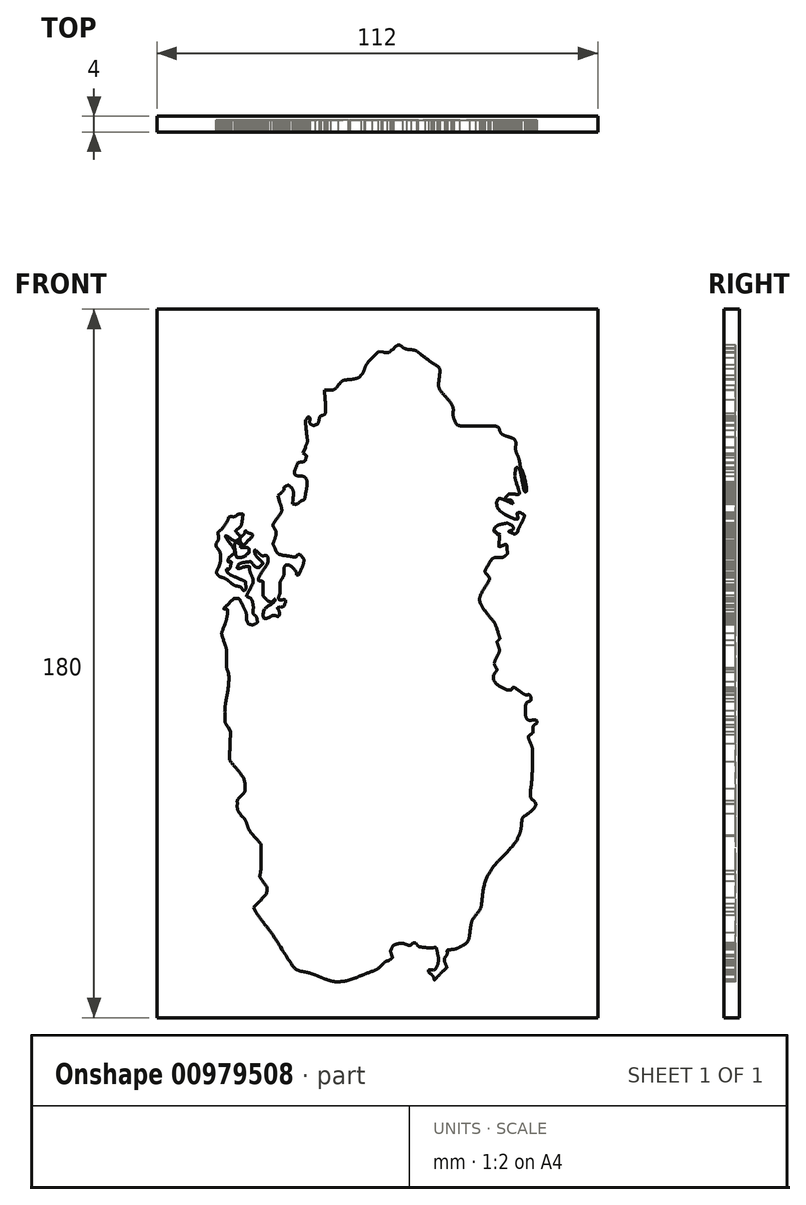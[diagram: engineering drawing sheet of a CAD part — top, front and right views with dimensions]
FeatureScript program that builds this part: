
annotation { "Feature Type Name" : "Feature", "Feature Type Description" : "" }
export const myFeature = defineFeature(function(context is Context, id is Id, definition is map)
    precondition{}
    {
        {
            var Q0;
            Q0=qCreatedBy(makeId("Front.planeOp"),FACE);
            var sketch = newSketch(context, id + "F0", { "sketchPlane" : qUnion([Q0])});
            skLineSegment(sketch, "E0.bottom", {"start": v(56, -90) * mm, "end": v(-56, -90) * mm});
            skLineSegment(sketch, "E0.top", {"start": v(56, 90) * mm, "end": v(-56, 90) * mm});
            skLineSegment(sketch, "E0.left", {"start": v(56, -90) * mm, "end": v(56, 90) * mm});
            skLineSegment(sketch, "E0.right", {"start": v(-56, -90) * mm, "end": v(-56, 90) * mm});
            skPoint(sketch, "E0.middle", {"position": v(0, 0) * mm});
            skLineSegment(sketch, "E1", {"start": v(-32.88, 19.2) * mm, "end": v(-32.1, 20.83) * mm});
            skLineSegment(sketch, "E2", {"start": v(-32.1, 20.83) * mm, "end": v(-32.57, 22.16) * mm});
            skLineSegment(sketch, "E3", {"start": v(-27.5, 16.63) * mm, "end": v(-26.83, 16.28) * mm});
            skLineSegment(sketch, "E4", {"start": v(-26.83, 16.28) * mm, "end": v(-26.97, 16.83) * mm});
            skLineSegment(sketch, "E5", {"start": v(-24.85, 15.67) * mm, "end": v(-25.4, 15.88) * mm});
            skLineSegment(sketch, "E6", {"start": v(-25.4, 15.88) * mm, "end": v(-25.34, 18.4) * mm});
            skLineSegment(sketch, "E7", {"start": v(-1.75, 78.04) * mm, "end": v(-0.2, 79.6) * mm});
            skLineSegment(sketch, "E8", {"start": v(-0.2, 79.6) * mm, "end": v(1.27, 79.6) * mm});
            skLineSegment(sketch, "E9", {"start": v(38.3, 44.26) * mm, "end": v(38.3, 43.17) * mm});
            skLineSegment(sketch, "E10", {"start": v(38.3, 43.17) * mm, "end": v(37.62, 43.24) * mm});
            skLineSegment(sketch, "E11", {"start": v(39.65, -31.25) * mm, "end": v(39.52, -33.83) * mm});
            skLineSegment(sketch, "E12", {"start": v(39.52, -33.83) * mm, "end": v(40.18, -34.42) * mm});
            skLineSegment(sketch, "E13", {"start": v(1.4, 79.08) * mm, "end": v(0.3, 79.22) * mm});
            skLineSegment(sketch, "E14", {"start": v(0.3, 79.22) * mm, "end": v(-1.23, 77.67) * mm});
            skLineSegment(sketch, "E15", {"start": v(-12.51, 69.45) * mm, "end": v(-13.4, 69.45) * mm});
            skLineSegment(sketch, "E16", {"start": v(-13.4, 69.45) * mm, "end": v(-13.27, 67.07) * mm});
            skLineSegment(sketch, "E17", {"start": v(-18.31, 54.9) * mm, "end": v(-18.88, 53.48) * mm});
            skLineSegment(sketch, "E18", {"start": v(-18.88, 53.48) * mm, "end": v(-18.43, 53.1) * mm});
            skLineSegment(sketch, "E19", {"start": v(-20.94, 40.45) * mm, "end": v(-21.55, 40.45) * mm});
            skLineSegment(sketch, "E20", {"start": v(-21.55, 40.45) * mm, "end": v(-21.44, 41.8) * mm});
            skLineSegment(sketch, "E21", {"start": v(-24.47, 43.3) * mm, "end": v(-25.23, 42.61) * mm});
            skLineSegment(sketch, "E22", {"start": v(-25.23, 42.61) * mm, "end": v(-24.8, 41.05) * mm});
            skLineSegment(sketch, "E23", {"start": v(-37.96, -16.18) * mm, "end": v(-37.29, -17.23) * mm});
            skLineSegment(sketch, "E24", {"start": v(-37.29, -17.23) * mm, "end": v(-37.41, -20.41) * mm});
            skLineSegment(sketch, "E25", {"start": v(-30.4, -60.92) * mm, "end": v(-31.42, -62.04) * mm});
            skLineSegment(sketch, "E26", {"start": v(-31.42, -62.04) * mm, "end": v(-30.9, -63.02) * mm});
            skLineSegment(sketch, "E27", {"start": v(-36.35, 33.14) * mm, "end": v(-36.7, 33.88) * mm});
            skLineSegment(sketch, "E28", {"start": v(-36.7, 33.88) * mm, "end": v(-35.92, 34.57) * mm});
            skLineSegment(sketch, "E29", {"start": v(-34.09, 31.43) * mm, "end": v(-34.09, 30.84) * mm});
            skLineSegment(sketch, "E30", {"start": v(-34.09, 30.84) * mm, "end": v(-33.35, 31.56) * mm});
            skFitSpline(sketch, "E31", {"points": [v(-13.45, -80.7) * mm, v(-14.26, -80.4) * mm, v(-15.79, -79.86) * mm, v(-16.84, -79.51) * mm]});
            skFitSpline(sketch, "E32", {"points": [v(-16.84, -79.51) * mm, v(-20.43, -78.33) * mm, v(-20.6, -78.25) * mm, v(-21.55, -77.26) * mm]});
            skFitSpline(sketch, "E33", {"points": [v(-21.55, -77.26) * mm, v(-22.07, -76.72) * mm, v(-23.66, -74.52) * mm, v(-25.09, -72.37) * mm]});
            skFitSpline(sketch, "E34", {"points": [v(-25.09, -72.37) * mm, v(-26.52, -70.21) * mm, v(-28.36, -67.6) * mm, v(-29.19, -66.55) * mm]});
            skFitSpline(sketch, "E35", {"points": [v(-29.19, -66.55) * mm, v(-30.6, -64.76) * mm, v(-31.97, -62.53) * mm, v(-31.97, -62.03) * mm]});
            skFitSpline(sketch, "E36", {"points": [v(-31.97, -62.03) * mm, v(-31.97, -61.91) * mm, v(-31.5, -61.27) * mm, v(-30.92, -60.6) * mm]});
            skFitSpline(sketch, "E37", {"points": [v(-30.92, -60.6) * mm, v(-29.85, -59.39) * mm, v(-29, -57.92) * mm, v(-29, -57.28) * mm]});
            skFitSpline(sketch, "E38", {"points": [v(-29, -57.28) * mm, v(-29, -57.08) * mm, v(-29.34, -56.3) * mm, v(-29.75, -55.53) * mm]});
            skFitSpline(sketch, "E39", {"points": [v(-29.75, -55.53) * mm, v(-30.57, -53.98) * mm, v(-30.63, -53.57) * mm, v(-30.2, -52.72) * mm]});
            skFitSpline(sketch, "E40", {"points": [v(-30.2, -52.72) * mm, v(-29.95, -52.26) * mm, v(-29.92, -51.55) * mm, v(-30.04, -49.29) * mm]});
            skFitSpline(sketch, "E41", {"points": [v(-30.04, -49.29) * mm, v(-30.2, -46.13) * mm, v(-30.12, -46.32) * mm, v(-32.34, -43.6) * mm]});
            skFitSpline(sketch, "E42", {"points": [v(-32.34, -43.6) * mm, v(-32.83, -43) * mm, v(-33.38, -42.01) * mm, v(-33.55, -41.42) * mm]});
            skFitSpline(sketch, "E43", {"points": [v(-33.55, -41.42) * mm, v(-33.73, -40.84) * mm, v(-34.2, -39.94) * mm, v(-34.62, -39.44) * mm]});
            skFitSpline(sketch, "E44", {"points": [v(-34.62, -39.44) * mm, v(-36.03, -37.71) * mm, v(-36.52, -35.97) * mm, v(-35.98, -34.56) * mm]});
            skFitSpline(sketch, "E45", {"points": [v(-35.98, -34.56) * mm, v(-35.86, -34.24) * mm, v(-35.38, -33.57) * mm, v(-34.92, -33.07) * mm]});
            skFitSpline(sketch, "E46", {"points": [v(-34.92, -33.07) * mm, v(-33.97, -32.03) * mm, v(-34, -32.17) * mm, v(-34.37, -30.78) * mm]});
            skFitSpline(sketch, "E47", {"points": [v(-34.37, -30.78) * mm, v(-34.75, -29.38) * mm, v(-35.2, -28.53) * mm, v(-36.46, -26.88) * mm]});
            skFitSpline(sketch, "E48", {"points": [v(-36.46, -26.88) * mm, v(-37.04, -26.13) * mm, v(-37.61, -25.27) * mm, v(-37.73, -24.97) * mm]});
            skFitSpline(sketch, "E49", {"points": [v(-37.73, -24.97) * mm, v(-37.97, -24.39) * mm, v(-38.06, -21.07) * mm, v(-37.9, -18.8) * mm]});
            skFitSpline(sketch, "E50", {"points": [v(-37.9, -18.8) * mm, v(-37.82, -17.55) * mm, v(-37.87, -17.35) * mm, v(-38.39, -16.67) * mm]});
            skFitSpline(sketch, "E51", {"points": [v(-38.39, -16.67) * mm, v(-39.51, -15.19) * mm, v(-39.6, -12.77) * mm, v(-38.72, -7.81) * mm]});
            skFitSpline(sketch, "E52", {"points": [v(-38.72, -7.81) * mm, v(-38.24, -5.14) * mm, v(-38.31, -2.1) * mm, v(-38.87, -1) * mm]});
            skFitSpline(sketch, "E53", {"points": [v(-38.87, -1) * mm, v(-39.1, -0.56) * mm, v(-39.11, -0.29) * mm, v(-38.94, 0.17) * mm]});
            skFitSpline(sketch, "E54", {"points": [v(-38.94, 0.17) * mm, v(-38.62, 1) * mm, v(-38.87, 3.38) * mm, v(-39.5, 5.38) * mm]});
            skFitSpline(sketch, "E55", {"points": [v(-39.5, 5.38) * mm, v(-39.78, 6.29) * mm, v(-40.01, 7.26) * mm, v(-40.01, 7.54) * mm]});
            skFitSpline(sketch, "E56", {"points": [v(-40.01, 7.54) * mm, v(-40.01, 7.83) * mm, v(-39.68, 9.05) * mm, v(-39.27, 10.27) * mm]});
            skFitSpline(sketch, "E57", {"points": [v(-39.27, 10.27) * mm, v(-38.41, 12.85) * mm, v(-38.39, 13.06) * mm, v(-38.96, 13.2) * mm]});
            skFitSpline(sketch, "E58", {"points": [v(-38.96, 13.2) * mm, v(-39.71, 13.4) * mm, v(-39.48, 14.32) * mm, v(-38.38, 15.5) * mm]});
            skFitSpline(sketch, "E59", {"points": [v(-38.38, 15.5) * mm, v(-36.83, 17.16) * mm, v(-35.68, 17.57) * mm, v(-34.74, 16.8) * mm]});
            skFitSpline(sketch, "E60", {"points": [v(-34.74, 16.8) * mm, v(-34.08, 16.26) * mm, v(-32.77, 13.22) * mm, v(-32.66, 11.98) * mm]});
            skFitSpline(sketch, "E61", {"points": [v(-32.66, 11.98) * mm, v(-32.55, 10.86) * mm, v(-32.37, 10.61) * mm, v(-31.6, 10.6) * mm]});
            skFitSpline(sketch, "E62", {"points": [v(-31.6, 10.6) * mm, v(-31, 10.6) * mm, v(-30.96, 11.24) * mm, v(-31.55, 11.77) * mm]});
            skFitSpline(sketch, "E63", {"points": [v(-31.55, 11.77) * mm, v(-31.84, 12.03) * mm, v(-31.97, 12.42) * mm, v(-31.97, 13) * mm]});
            skFitSpline(sketch, "E64", {"points": [v(-31.97, 13) * mm, v(-31.97, 14.32) * mm, v(-32.62, 16.12) * mm, v(-33.18, 16.38) * mm]});
            skFitSpline(sketch, "E65", {"points": [v(-33.18, 16.38) * mm, v(-33.86, 16.69) * mm, v(-33.8, 17.27) * mm, v(-32.88, 19.2) * mm]});
            skFitSpline(sketch, "E66", {"points": [v(-32.57, 22.16) * mm, v(-32.82, 22.9) * mm, v(-33.03, 23.65) * mm, v(-33.03, 23.83) * mm]});
            skFitSpline(sketch, "E67", {"points": [v(-33.03, 23.83) * mm, v(-33.03, 24.1) * mm, v(-33.14, 24.14) * mm, v(-33.5, 24.01) * mm]});
            skFitSpline(sketch, "E68", {"points": [v(-33.5, 24.01) * mm, v(-33.77, 23.92) * mm, v(-34.4, 23.84) * mm, v(-34.93, 23.84) * mm]});
            skFitSpline(sketch, "E69", {"points": [v(-34.93, 23.84) * mm, v(-35.84, 23.83) * mm, v(-35.89, 23.86) * mm, v(-35.95, 24.48) * mm]});
            skFitSpline(sketch, "E70", {"points": [v(-35.95, 24.48) * mm, v(-36.05, 25.55) * mm, v(-34.78, 26.27) * mm, v(-32.78, 26.27) * mm]});
            skFitSpline(sketch, "E71", {"points": [v(-32.78, 26.27) * mm, v(-31.93, 26.27) * mm, v(-31.64, 26.16) * mm, v(-31.1, 25.65) * mm]});
            skFitSpline(sketch, "E72", {"points": [v(-31.1, 25.65) * mm, v(-30.75, 25.3) * mm, v(-30.32, 25.08) * mm, v(-30.15, 25.14) * mm]});
            skFitSpline(sketch, "E73", {"points": [v(-30.15, 25.14) * mm, v(-29.7, 25.31) * mm, v(-29.77, 25.47) * mm, v(-30.7, 26.37) * mm]});
            skFitSpline(sketch, "E74", {"points": [v(-30.7, 26.37) * mm, v(-31.5, 27.15) * mm, v(-31.55, 27.27) * mm, v(-31.55, 28.43) * mm]});
            skFitSpline(sketch, "E75", {"points": [v(-31.55, 28.43) * mm, v(-31.55, 29.6) * mm, v(-31.52, 29.65) * mm, v(-31.02, 29.65) * mm]});
            skFitSpline(sketch, "E76", {"points": [v(-31.02, 29.65) * mm, v(-30.7, 29.65) * mm, v(-30.49, 29.53) * mm, v(-30.49, 29.36) * mm]});
            skFitSpline(sketch, "E77", {"points": [v(-30.49, 29.36) * mm, v(-30.49, 28.94) * mm, v(-28.82, 27.75) * mm, v(-28.24, 27.75) * mm]});
            skFitSpline(sketch, "E78", {"points": [v(-28.24, 27.75) * mm, v(-27.83, 27.75) * mm, v(-27.75, 27.6) * mm, v(-27.62, 26.6) * mm]});
            skFitSpline(sketch, "E79", {"points": [v(-27.62, 26.6) * mm, v(-27.46, 25.26) * mm, v(-27.66, 24.55) * mm, v(-28.57, 23.22) * mm]});
            skFitSpline(sketch, "E80", {"points": [v(-28.57, 23.22) * mm, v(-29.21, 22.29) * mm, v(-29.4, 21.61) * mm, v(-29.02, 21.61) * mm]});
            skFitSpline(sketch, "E81", {"points": [v(-29.02, 21.61) * mm, v(-28.66, 21.61) * mm, v(-28.35, 20.18) * mm, v(-28.49, 19.14) * mm]});
            skFitSpline(sketch, "E82", {"points": [v(-28.49, 19.14) * mm, v(-28.66, 17.84) * mm, v(-28.36, 17.07) * mm, v(-27.5, 16.63) * mm]});
            skFitSpline(sketch, "E83", {"points": [v(-26.97, 16.83) * mm, v(-27.1, 17.33) * mm, v(-27.05, 17.38) * mm, v(-26.5, 17.38) * mm]});
            skFitSpline(sketch, "E84", {"points": [v(-26.5, 17.38) * mm, v(-25.81, 17.38) * mm, v(-25.62, 17.08) * mm, v(-25.62, 16.04) * mm]});
            skFitSpline(sketch, "E85", {"points": [v(-25.62, 16.04) * mm, v(-25.62, 15.5) * mm, v(-25.82, 15.19) * mm, v(-26.56, 14.52) * mm]});
            skFitSpline(sketch, "E86", {"points": [v(-26.56, 14.52) * mm, v(-27.09, 14.05) * mm, v(-27.58, 13.4) * mm, v(-27.66, 13.06) * mm]});
            skFitSpline(sketch, "E87", {"points": [v(-27.66, 13.06) * mm, v(-27.79, 12.49) * mm, v(-27.76, 12.45) * mm, v(-27.3, 12.58) * mm]});
            skFitSpline(sketch, "E88", {"points": [v(-27.3, 12.58) * mm, v(-27.01, 12.65) * mm, v(-26.47, 12.72) * mm, v(-26.09, 12.72) * mm]});
            skFitSpline(sketch, "E89", {"points": [v(-26.09, 12.72) * mm, v(-25.47, 12.72) * mm, v(-25.42, 12.76) * mm, v(-25.61, 13.13) * mm]});
            skFitSpline(sketch, "E90", {"points": [v(-25.61, 13.13) * mm, v(-26.02, 13.88) * mm, v(-25.88, 14.6) * mm, v(-25.31, 14.75) * mm]});
            skFitSpline(sketch, "E91", {"points": [v(-25.31, 14.75) * mm, v(-25.03, 14.82) * mm, v(-24.68, 15.01) * mm, v(-24.55, 15.17) * mm]});
            skFitSpline(sketch, "E92", {"points": [v(-24.55, 15.17) * mm, v(-24.35, 15.4) * mm, v(-24.42, 15.5) * mm, v(-24.85, 15.67) * mm]});
            skFitSpline(sketch, "E93", {"points": [v(-25.34, 18.4) * mm, v(-25.28, 20.49) * mm, v(-25.2, 21.05) * mm, v(-24.84, 21.66) * mm]});
            skFitSpline(sketch, "E94", {"points": [v(-24.84, 21.66) * mm, v(-24.6, 22.07) * mm, v(-24.33, 22.91) * mm, v(-24.25, 23.54) * mm]});
            skFitSpline(sketch, "E95", {"points": [v(-24.25, 23.54) * mm, v(-24.05, 24.98) * mm, v(-23.67, 25.42) * mm, v(-22.64, 25.42) * mm]});
            skFitSpline(sketch, "E96", {"points": [v(-22.64, 25.42) * mm, v(-21.97, 25.42) * mm, v(-21.73, 25.28) * mm, v(-21.09, 24.54) * mm]});
            skFitSpline(sketch, "E97", {"points": [v(-21.09, 24.54) * mm, v(-20.67, 24.05) * mm, v(-20.32, 23.55) * mm, v(-20.32, 23.43) * mm]});
            skFitSpline(sketch, "E98", {"points": [v(-20.32, 23.43) * mm, v(-20.3, 22.93) * mm, v(-19.5, 25.15) * mm, v(-19.5, 25.74) * mm]});
            skFitSpline(sketch, "E99", {"points": [v(-19.5, 25.74) * mm, v(-19.48, 26.68) * mm, v(-19.75, 27) * mm, v(-20.27, 26.68) * mm]});
            skFitSpline(sketch, "E100", {"points": [v(-20.27, 26.68) * mm, v(-20.84, 26.32) * mm, v(-23.7, 26.75) * mm, v(-24.99, 27.38) * mm]});
            skFitSpline(sketch, "E101", {"points": [v(-24.99, 27.38) * mm, v(-26.7, 28.23) * mm, v(-27.27, 29.95) * mm, v(-26.55, 32.07) * mm]});
            skFitSpline(sketch, "E102", {"points": [v(-26.55, 32.07) * mm, v(-26.23, 33) * mm, v(-26.23, 33.13) * mm, v(-26.58, 33.9) * mm]});
            skFitSpline(sketch, "E103", {"points": [v(-26.58, 33.9) * mm, v(-27.04, 34.91) * mm, v(-26.9, 36) * mm, v(-26.2, 36.92) * mm]});
            skFitSpline(sketch, "E104", {"points": [v(-26.2, 36.92) * mm, v(-24.96, 38.54) * mm, v(-24.76, 39.42) * mm, v(-25.3, 40.73) * mm]});
            skFitSpline(sketch, "E105", {"points": [v(-25.3, 40.73) * mm, v(-25.48, 41.15) * mm, v(-25.62, 41.87) * mm, v(-25.62, 42.33) * mm]});
            skFitSpline(sketch, "E106", {"points": [v(-25.62, 42.33) * mm, v(-25.62, 43.02) * mm, v(-25.5, 43.25) * mm, v(-24.99, 43.62) * mm]});
            skFitSpline(sketch, "E107", {"points": [v(-24.99, 43.62) * mm, v(-24.64, 43.87) * mm, v(-24.35, 44.26) * mm, v(-24.35, 44.48) * mm]});
            skFitSpline(sketch, "E108", {"points": [v(-24.35, 44.48) * mm, v(-24.35, 45.6) * mm, v(-22.43, 46.16) * mm, v(-21.62, 45.29) * mm]});
            skFitSpline(sketch, "E109", {"points": [v(-21.62, 45.29) * mm, v(-21.1, 44.74) * mm, v(-20.66, 42.78) * mm, v(-20.82, 41.8) * mm]});
            skFitSpline(sketch, "E110", {"points": [v(-20.82, 41.8) * mm, v(-20.95, 40.98) * mm, v(-20.5, 40.8) * mm, v(-20.12, 41.5) * mm]});
            skFitSpline(sketch, "E111", {"points": [v(-20.12, 41.5) * mm, v(-20, 41.74) * mm, v(-19.7, 41.93) * mm, v(-19.48, 41.93) * mm]});
            skFitSpline(sketch, "E112", {"points": [v(-19.48, 41.93) * mm, v(-19.2, 41.93) * mm, v(-19.03, 42.12) * mm, v(-18.95, 42.51) * mm]});
            skFitSpline(sketch, "E113", {"points": [v(-18.95, 42.51) * mm, v(-18.9, 42.83) * mm, v(-18.75, 43.5) * mm, v(-18.63, 44) * mm]});
            skFitSpline(sketch, "E114", {"points": [v(-18.63, 44) * mm, v(-18.15, 46.1) * mm, v(-18.46, 46.83) * mm, v(-19.95, 47.1) * mm]});
            skFitSpline(sketch, "E115", {"points": [v(-19.95, 47.1) * mm, v(-21.37, 47.35) * mm, v(-21.68, 48.31) * mm, v(-21.02, 50.45) * mm]});
            skFitSpline(sketch, "E116", {"points": [v(-21.02, 50.45) * mm, v(-20.67, 51.58) * mm, v(-20.6, 51.66) * mm, v(-20, 51.67) * mm]});
            skFitSpline(sketch, "E117", {"points": [v(-20, 51.67) * mm, v(-19.64, 51.67) * mm, v(-19.17, 51.8) * mm, v(-18.94, 51.97) * mm]});
            skFitSpline(sketch, "E118", {"points": [v(-18.94, 51.97) * mm, v(-18.56, 52.25) * mm, v(-18.55, 52.28) * mm, v(-18.9, 52.67) * mm]});
            skFitSpline(sketch, "E119", {"points": [v(-18.9, 52.67) * mm, v(-19.36, 53.18) * mm, v(-19.37, 53.99) * mm, v(-18.93, 55) * mm]});
            skFitSpline(sketch, "E120", {"points": [v(-18.93, 55) * mm, v(-18.26, 56.57) * mm, v(-18.22, 56.96) * mm, v(-18.55, 58.71) * mm]});
            skFitSpline(sketch, "E121", {"points": [v(-18.55, 58.71) * mm, v(-19.05, 61.35) * mm, v(-18.66, 63.1) * mm, v(-17.57, 63.1) * mm]});
            skFitSpline(sketch, "E122", {"points": [v(-17.57, 63.1) * mm, v(-17.13, 63.1) * mm, v(-16.93, 62.86) * mm, v(-16.62, 61.94) * mm]});
            skFitSpline(sketch, "E123", {"points": [v(-16.62, 61.94) * mm, v(-16.19, 60.62) * mm, v(-15.25, 61.36) * mm, v(-15.25, 63.03) * mm]});
            skFitSpline(sketch, "E124", {"points": [v(-15.25, 63.03) * mm, v(-15.25, 63.72) * mm, v(-15.21, 63.77) * mm, v(-14.72, 63.65) * mm]});
            skFitSpline(sketch, "E125", {"points": [v(-14.72, 63.65) * mm, v(-13.88, 63.44) * mm, v(-13.7, 64.21) * mm, v(-13.86, 67.25) * mm]});
            skFitSpline(sketch, "E126", {"points": [v(-13.86, 67.25) * mm, v(-14.01, 70.15) * mm, v(-14.06, 70.07) * mm, v(-12.21, 70.08) * mm]});
            skFitSpline(sketch, "E127", {"points": [v(-12.21, 70.08) * mm, v(-11.52, 70.08) * mm, v(-11.25, 70.23) * mm, v(-10.4, 71.12) * mm]});
            skFitSpline(sketch, "E128", {"points": [v(-10.4, 71.12) * mm, v(-9.38, 72.18) * mm, v(-9.03, 72.34) * mm, v(-6.52, 72.84) * mm]});
            skFitSpline(sketch, "E129", {"points": [v(-6.52, 72.84) * mm, v(-4.93, 73.15) * mm, v(-4.21, 73.78) * mm, v(-3.7, 75.27) * mm]});
            skFitSpline(sketch, "E130", {"points": [v(-3.7, 75.27) * mm, v(-3.38, 76.2) * mm, v(-2.96, 76.8) * mm, v(-1.75, 78.04) * mm]});
            skFitSpline(sketch, "E131", {"points": [v(1.27, 79.6) * mm, v(2.66, 79.6) * mm, v(2.79, 79.65) * mm, v(3.57, 80.36) * mm]});
            skFitSpline(sketch, "E132", {"points": [v(3.57, 80.36) * mm, v(4.72, 81.4) * mm, v(5.62, 81.51) * mm, v(6.84, 80.8) * mm]});
            skFitSpline(sketch, "E133", {"points": [v(6.84, 80.8) * mm, v(7.4, 80.48) * mm, v(8.11, 80.24) * mm, v(8.56, 80.24) * mm]});
            skFitSpline(sketch, "E134", {"points": [v(8.56, 80.24) * mm, v(9.65, 80.24) * mm, v(10.66, 79.76) * mm, v(12.03, 78.58) * mm]});
            skFitSpline(sketch, "E135", {"points": [v(12.03, 78.58) * mm, v(12.68, 78.02) * mm, v(13.76, 77.21) * mm, v(14.43, 76.8) * mm]});
            skFitSpline(sketch, "E136", {"points": [v(14.43, 76.8) * mm, v(16.07, 75.75) * mm, v(16.3, 75.23) * mm, v(16.26, 72.68) * mm]});
            skFitSpline(sketch, "E137", {"points": [v(16.26, 72.68) * mm, v(16.21, 70.3) * mm, v(16.3, 70.06) * mm, v(17.99, 67.97) * mm]});
            skFitSpline(sketch, "E138", {"points": [v(17.99, 67.97) * mm, v(19.34, 66.28) * mm, v(19.58, 65.73) * mm, v(19.78, 63.84) * mm]});
            skFitSpline(sketch, "E139", {"points": [v(19.78, 63.84) * mm, v(19.97, 61.97) * mm, v(20.1, 61.75) * mm, v(21.2, 61.28) * mm]});
            skFitSpline(sketch, "E140", {"points": [v(21.2, 61.28) * mm, v(21.95, 60.97) * mm, v(22.77, 60.9) * mm, v(25.95, 60.87) * mm]});
            skFitSpline(sketch, "E141", {"points": [v(25.95, 60.87) * mm, v(29.47, 60.83) * mm, v(29.87, 60.8) * mm, v(30.78, 60.35) * mm]});
            skFitSpline(sketch, "E142", {"points": [v(30.78, 60.35) * mm, v(31.33, 60.09) * mm, v(31.82, 59.71) * mm, v(31.88, 59.53) * mm]});
            skFitSpline(sketch, "E143", {"points": [v(31.88, 59.53) * mm, v(32.1, 58.78) * mm, v(32.32, 58.58) * mm, v(33.34, 58.19) * mm]});
            skFitSpline(sketch, "E144", {"points": [v(33.34, 58.19) * mm, v(35, 57.54) * mm, v(35.47, 56.96) * mm, v(35.61, 55.41) * mm]});
            skFitSpline(sketch, "E145", {"points": [v(35.61, 55.41) * mm, v(35.68, 54.7) * mm, v(35.93, 53.67) * mm, v(36.17, 53.15) * mm]});
            skFitSpline(sketch, "E146", {"points": [v(36.17, 53.15) * mm, v(36.4, 52.63) * mm, v(36.6, 51.94) * mm, v(36.6, 51.62) * mm]});
            skFitSpline(sketch, "E147", {"points": [v(36.6, 51.62) * mm, v(36.6, 51.3) * mm, v(36.8, 50.55) * mm, v(37.02, 49.93) * mm]});
            skFitSpline(sketch, "E148", {"points": [v(37.02, 49.93) * mm, v(37.7, 48.08) * mm, v(38.3, 45.42) * mm, v(38.3, 44.26) * mm]});
            skFitSpline(sketch, "E149", {"points": [v(37.62, 43.24) * mm, v(36.87, 43.31) * mm, v(36.86, 43.33) * mm, v(36.05, 46.9) * mm]});
            skFitSpline(sketch, "E150", {"points": [v(36.05, 46.9) * mm, v(35.75, 48.23) * mm, v(35.65, 48.45) * mm, v(35.6, 47.92) * mm]});
            skFitSpline(sketch, "E151", {"points": [v(35.6, 47.92) * mm, v(35.56, 47.55) * mm, v(35.72, 46.61) * mm, v(35.96, 45.84) * mm]});
            skFitSpline(sketch, "E152", {"points": [v(35.96, 45.84) * mm, v(36.2, 45.06) * mm, v(36.4, 44.16) * mm, v(36.4, 43.83) * mm]});
            skFitSpline(sketch, "E153", {"points": [v(36.4, 43.83) * mm, v(36.4, 42.72) * mm, v(36.23, 42.57) * mm, v(35.04, 42.57) * mm]});
            skFitSpline(sketch, "E154", {"points": [v(35.04, 42.57) * mm, v(34.35, 42.57) * mm, v(33.78, 42.44) * mm, v(33.53, 42.23) * mm]});
            skFitSpline(sketch, "E155", {"points": [v(33.53, 42.23) * mm, v(33.14, 41.92) * mm, v(33.15, 41.9) * mm, v(33.78, 42.01) * mm]});
            skFitSpline(sketch, "E156", {"points": [v(33.78, 42.01) * mm, v(34.37, 42.1) * mm, v(34.48, 42.05) * mm, v(34.7, 41.5) * mm]});
            skFitSpline(sketch, "E157", {"points": [v(34.7, 41.5) * mm, v(35.23, 40.23) * mm, v(34.46, 39.89) * mm, v(32.77, 40.66) * mm]});
            skFitSpline(sketch, "E158", {"points": [v(32.77, 40.66) * mm, v(30, 41.91) * mm, v(30.46, 40.26) * mm, v(33.3, 38.77) * mm]});
            skFitSpline(sketch, "E159", {"points": [v(33.3, 38.77) * mm, v(34.7, 38.04) * mm, v(35.03, 37.98) * mm, v(35.2, 38.44) * mm]});
            skFitSpline(sketch, "E160", {"points": [v(35.2, 38.44) * mm, v(35.4, 38.97) * mm, v(36.94, 38.86) * mm, v(37.34, 38.29) * mm]});
            skFitSpline(sketch, "E161", {"points": [v(37.34, 38.29) * mm, v(37.8, 37.64) * mm, v(37.75, 36.5) * mm, v(37.25, 35.69) * mm]});
            skFitSpline(sketch, "E162", {"points": [v(37.25, 35.69) * mm, v(37.01, 35.31) * mm, v(36.68, 34.6) * mm, v(36.5, 34.09) * mm]});
            skFitSpline(sketch, "E163", {"points": [v(36.5, 34.09) * mm, v(36.07, 32.87) * mm, v(35.62, 32.4) * mm, v(34.86, 32.4) * mm]});
            skFitSpline(sketch, "E164", {"points": [v(34.86, 32.4) * mm, v(34.06, 32.4) * mm, v(32.85, 32.98) * mm, v(32.57, 33.5) * mm]});
            skFitSpline(sketch, "E165", {"points": [v(32.57, 33.5) * mm, v(32.35, 33.9) * mm, v(32.37, 33.91) * mm, v(33.4, 34.23) * mm]});
            skFitSpline(sketch, "E166", {"points": [v(33.4, 34.23) * mm, v(33.55, 34.27) * mm, v(33.64, 34.43) * mm, v(33.6, 34.58) * mm]});
            skFitSpline(sketch, "E167", {"points": [v(33.6, 34.58) * mm, v(33.47, 34.97) * mm, v(32.1, 35.02) * mm, v(31.26, 34.66) * mm]});
            skFitSpline(sketch, "E168", {"points": [v(31.26, 34.66) * mm, v(30.63, 34.4) * mm, v(30.54, 34.27) * mm, v(30.63, 33.8) * mm]});
            skFitSpline(sketch, "E169", {"points": [v(30.63, 33.8) * mm, v(30.71, 33.37) * mm, v(30.83, 33.27) * mm, v(31.13, 33.37) * mm]});
            skFitSpline(sketch, "E170", {"points": [v(31.13, 33.37) * mm, v(31.68, 33.54) * mm, v(31.8, 33.13) * mm, v(31.57, 31.7) * mm]});
            skFitSpline(sketch, "E171", {"points": [v(31.57, 31.7) * mm, v(31.47, 31.04) * mm, v(31.4, 30.5) * mm, v(31.43, 30.5) * mm]});
            skFitSpline(sketch, "E172", {"points": [v(31.43, 30.5) * mm, v(31.46, 30.5) * mm, v(31.82, 30.65) * mm, v(32.25, 30.82) * mm]});
            skFitSpline(sketch, "E173", {"points": [v(32.25, 30.82) * mm, v(33.01, 31.14) * mm, v(33.02, 31.14) * mm, v(33.26, 30.56) * mm]});
            skFitSpline(sketch, "E174", {"points": [v(33.26, 30.56) * mm, v(33.39, 30.24) * mm, v(33.5, 29.43) * mm, v(33.52, 28.77) * mm]});
            skFitSpline(sketch, "E175", {"points": [v(33.52, 28.77) * mm, v(33.55, 27.14) * mm, v(33.03, 26.57) * mm, v(31.4, 26.43) * mm]});
            skFitSpline(sketch, "E176", {"points": [v(31.4, 26.43) * mm, v(29.99, 26.32) * mm, v(29.27, 25.83) * mm, v(28.59, 24.5) * mm]});
            skFitSpline(sketch, "E177", {"points": [v(28.59, 24.5) * mm, v(28.09, 23.52) * mm, v(28.09, 23.5) * mm, v(28.46, 22.8) * mm]});
            skFitSpline(sketch, "E178", {"points": [v(28.46, 22.8) * mm, v(29.02, 21.76) * mm, v(28.8, 20.5) * mm, v(27.76, 18.77) * mm]});
            skFitSpline(sketch, "E179", {"points": [v(27.76, 18.77) * mm, v(26.26, 16.28) * mm, v(26.34, 15.6) * mm, v(28.5, 12.89) * mm]});
            skFitSpline(sketch, "E180", {"points": [v(28.5, 12.89) * mm, v(30.07, 10.9) * mm, v(30.64, 9.85) * mm, v(31.32, 7.7) * mm]});
            skFitSpline(sketch, "E181", {"points": [v(31.32, 7.7) * mm, v(31.79, 6.2) * mm, v(31.8, 6.14) * mm, v(31.41, 5.73) * mm]});
            skFitSpline(sketch, "E182", {"points": [v(31.41, 5.73) * mm, v(31.08, 5.36) * mm, v(31.06, 5.2) * mm, v(31.28, 4.6) * mm]});
            skFitSpline(sketch, "E183", {"points": [v(31.28, 4.6) * mm, v(31.65, 3.58) * mm, v(31.59, 2.92) * mm, v(31, 1.59) * mm]});
            skFitSpline(sketch, "E184", {"points": [v(31, 1.59) * mm, v(30.4, 0.22) * mm, v(30.37, 0) * mm, v(30.73, -0.98) * mm]});
            skFitSpline(sketch, "E185", {"points": [v(30.73, -0.98) * mm, v(30.96, -1.6) * mm, v(30.93, -1.79) * mm, v(30.48, -2.62) * mm]});
            skFitSpline(sketch, "E186", {"points": [v(30.48, -2.62) * mm, v(29.76, -3.92) * mm, v(30.03, -4.4) * mm, v(31.97, -5.39) * mm]});
            skFitSpline(sketch, "E187", {"points": [v(31.97, -5.39) * mm, v(33.32, -6.07) * mm, v(33.55, -6.12) * mm, v(34.1, -5.9) * mm]});
            skFitSpline(sketch, "E188", {"points": [v(34.1, -5.9) * mm, v(34.89, -5.57) * mm, v(35.48, -5.74) * mm, v(36.67, -6.64) * mm]});
            skFitSpline(sketch, "E189", {"points": [v(36.67, -6.64) * mm, v(37.21, -7.06) * mm, v(37.94, -7.45) * mm, v(38.28, -7.52) * mm]});
            skFitSpline(sketch, "E190", {"points": [v(38.28, -7.52) * mm, v(38.74, -7.61) * mm, v(38.97, -7.82) * mm, v(39.14, -8.29) * mm]});
            skFitSpline(sketch, "E191", {"points": [v(39.14, -8.29) * mm, v(39.46, -9.22) * mm, v(39.43, -9.36) * mm, v(38.73, -10.24) * mm]});
            skFitSpline(sketch, "E192", {"points": [v(38.73, -10.24) * mm, v(37.95, -11.22) * mm, v(37.9, -12.13) * mm, v(38.57, -13.12) * mm]});
            skFitSpline(sketch, "E193", {"points": [v(38.57, -13.12) * mm, v(38.94, -13.67) * mm, v(39.23, -13.86) * mm, v(39.79, -13.91) * mm]});
            skFitSpline(sketch, "E194", {"points": [v(39.79, -13.91) * mm, v(40.2, -13.95) * mm, v(40.6, -14.1) * mm, v(40.68, -14.23) * mm]});
            skFitSpline(sketch, "E195", {"points": [v(40.68, -14.23) * mm, v(40.98, -14.7) * mm, v(40.84, -15.58) * mm, v(40.4, -15.98) * mm]});
            skFitSpline(sketch, "E196", {"points": [v(40.4, -15.98) * mm, v(40.04, -16.3) * mm, v(39.97, -16.56) * mm, v(40.05, -17.26) * mm]});
            skFitSpline(sketch, "E197", {"points": [v(40.05, -17.26) * mm, v(40.14, -18.03) * mm, v(40.09, -18.17) * mm, v(39.65, -18.37) * mm]});
            skFitSpline(sketch, "E198", {"points": [v(39.65, -18.37) * mm, v(39.06, -18.64) * mm, v(39.03, -18.9) * mm, v(39.5, -20) * mm]});
            skFitSpline(sketch, "E199", {"points": [v(39.5, -20) * mm, v(39.77, -20.67) * mm, v(39.83, -21.57) * mm, v(39.81, -24.74) * mm]});
            skFitSpline(sketch, "E200", {"points": [v(39.81, -24.74) * mm, v(39.8, -26.9) * mm, v(39.73, -29.82) * mm, v(39.65, -31.25) * mm]});
            skFitSpline(sketch, "E201", {"points": [v(40.18, -34.42) * mm, v(40.54, -34.74) * mm, v(40.84, -35.18) * mm, v(40.84, -35.41) * mm]});
            skFitSpline(sketch, "E202", {"points": [v(40.84, -35.41) * mm, v(40.84, -36.27) * mm, v(39.96, -37.65) * mm, v(38.92, -38.41) * mm]});
            skFitSpline(sketch, "E203", {"points": [v(38.92, -38.41) * mm, v(37.63, -39.36) * mm, v(37.28, -40) * mm, v(37.05, -41.89) * mm]});
            skFitSpline(sketch, "E204", {"points": [v(37.05, -41.89) * mm, v(36.94, -42.7) * mm, v(36.66, -43.77) * mm, v(36.42, -44.27) * mm]});
            skFitSpline(sketch, "E205", {"points": [v(36.42, -44.27) * mm, v(35.96, -45.22) * mm, v(33.78, -47.87) * mm, v(31.3, -50.5) * mm]});
            skFitSpline(sketch, "E206", {"points": [v(31.3, -50.5) * mm, v(29.02, -52.92) * mm, v(27.8, -55.66) * mm, v(27.2, -59.77) * mm]});
            skFitSpline(sketch, "E207", {"points": [v(27.2, -59.77) * mm, v(26.85, -62.13) * mm, v(26.75, -62.37) * mm, v(25.14, -65) * mm]});
            skFitSpline(sketch, "E208", {"points": [v(25.14, -65) * mm, v(24.58, -65.91) * mm, v(24.35, -66.6) * mm, v(24.16, -67.9) * mm]});
            skFitSpline(sketch, "E209", {"points": [v(24.16, -67.9) * mm, v(23.88, -69.93) * mm, v(23.36, -71.03) * mm, v(22.29, -71.92) * mm]});
            skFitSpline(sketch, "E210", {"points": [v(22.29, -71.92) * mm, v(21.43, -72.63) * mm, v(19.94, -73.22) * mm, v(19, -73.22) * mm]});
            skFitSpline(sketch, "E211", {"points": [v(19, -73.22) * mm, v(18.6, -73.22) * mm, v(18.4, -73.32) * mm, v(18.4, -73.56) * mm]});
            skFitSpline(sketch, "E212", {"points": [v(18.4, -73.56) * mm, v(18.4, -73.75) * mm, v(18.21, -74.22) * mm, v(17.97, -74.6) * mm]});
            skFitSpline(sketch, "E213", {"points": [v(17.97, -74.6) * mm, v(17.57, -75.26) * mm, v(17.56, -75.35) * mm, v(17.87, -76.08) * mm]});
            skFitSpline(sketch, "E214", {"points": [v(17.87, -76.08) * mm, v(18.34, -77.22) * mm, v(18.3, -77.38) * mm, v(17.14, -78.58) * mm]});
            skFitSpline(sketch, "E215", {"points": [v(17.14, -78.58) * mm, v(16.56, -79.18) * mm, v(15.87, -79.93) * mm, v(15.6, -80.25) * mm]});
            skFitSpline(sketch, "E216", {"points": [v(15.6, -80.25) * mm, v(15.34, -80.56) * mm, v(14.86, -80.88) * mm, v(14.54, -80.96) * mm]});
            skFitSpline(sketch, "E217", {"points": [v(14.54, -80.96) * mm, v(14.03, -81.08) * mm, v(13.96, -81.03) * mm, v(13.96, -80.56) * mm]});
            skFitSpline(sketch, "E218", {"points": [v(13.96, -80.56) * mm, v(13.96, -80.25) * mm, v(13.75, -79.86) * mm, v(13.47, -79.63) * mm]});
            skFitSpline(sketch, "E219", {"points": [v(13.47, -79.63) * mm, v(12.33, -78.73) * mm, v(12.3, -77.45) * mm, v(13.44, -77.45) * mm]});
            skFitSpline(sketch, "E220", {"points": [v(13.44, -77.45) * mm, v(14.2, -77.45) * mm, v(15.11, -76) * mm, v(14.94, -75.07) * mm]});
            skFitSpline(sketch, "E221", {"points": [v(14.94, -75.07) * mm, v(14.87, -74.7) * mm, v(14.75, -74.02) * mm, v(14.67, -73.57) * mm]});
            skFitSpline(sketch, "E222", {"points": [v(14.67, -73.57) * mm, v(14.58, -73.02) * mm, v(14.45, -72.8) * mm, v(14.25, -72.88) * mm]});
            skFitSpline(sketch, "E223", {"points": [v(14.25, -72.88) * mm, v(14.1, -72.94) * mm, v(13.13, -72.88) * mm, v(12.11, -72.76) * mm]});
            skFitSpline(sketch, "E224", {"points": [v(12.11, -72.76) * mm, v(10.8, -72.6) * mm, v(10.12, -72.4) * mm, v(9.8, -72.1) * mm]});
            skFitSpline(sketch, "E225", {"points": [v(9.8, -72.1) * mm, v(9.32, -71.67) * mm, v(8.88, -71.75) * mm, v(8.88, -72.28) * mm]});
            skFitSpline(sketch, "E226", {"points": [v(8.88, -72.28) * mm, v(8.88, -72.66) * mm, v(8.5, -72.65) * mm, v(7.82, -72.26) * mm]});
            skFitSpline(sketch, "E227", {"points": [v(7.82, -72.26) * mm, v(7.11, -71.86) * mm, v(5.83, -71.87) * mm, v(4.94, -72.29) * mm]});
            skFitSpline(sketch, "E228", {"points": [v(4.94, -72.29) * mm, v(4.16, -72.66) * mm, v(4.18, -72.61) * mm, v(4.14, -74.27) * mm]});
            skFitSpline(sketch, "E229", {"points": [v(4.14, -74.27) * mm, v(4.12, -75.43) * mm, v(4.11, -75.44) * mm, v(3.17, -75.91) * mm]});
            skFitSpline(sketch, "E230", {"points": [v(3.17, -75.91) * mm, v(2.65, -76.18) * mm, v(1.84, -76.77) * mm, v(1.36, -77.24) * mm]});
            skFitSpline(sketch, "E231", {"points": [v(1.36, -77.24) * mm, v(0.68, -77.91) * mm, v(-0.19, -78.37) * mm, v(-2.67, -79.37) * mm]});
            skFitSpline(sketch, "E232", {"points": [v(-2.67, -79.37) * mm, v(-6.5, -80.92) * mm, v(-7.82, -81.25) * mm, v(-10.17, -81.25) * mm]});
            skFitSpline(sketch, "E233", {"points": [v(-10.17, -81.25) * mm, v(-11.59, -81.25) * mm, v(-12.28, -81.13) * mm, v(-13.45, -80.7) * mm]});
            skFitSpline(sketch, "E234", {"points": [v(-6.84, -80.3) * mm, v(-6.29, -80.14) * mm, v(-4.56, -79.5) * mm, v(-3, -78.88) * mm]});
            skFitSpline(sketch, "E235", {"points": [v(-3, -78.88) * mm, v(-0.66, -77.96) * mm, v(0.05, -77.57) * mm, v(1.08, -76.65) * mm]});
            skFitSpline(sketch, "E236", {"points": [v(1.08, -76.65) * mm, v(1.77, -76.04) * mm, v(2.46, -75.54) * mm, v(2.62, -75.54) * mm]});
            skFitSpline(sketch, "E237", {"points": [v(2.62, -75.54) * mm, v(2.78, -75.54) * mm, v(3.12, -75.37) * mm, v(3.38, -75.16) * mm]});
            skFitSpline(sketch, "E238", {"points": [v(3.38, -75.16) * mm, v(3.8, -74.81) * mm, v(3.83, -74.72) * mm, v(3.59, -73.93) * mm]});
            skFitSpline(sketch, "E239", {"points": [v(3.59, -73.93) * mm, v(3.4, -73.28) * mm, v(3.39, -72.96) * mm, v(3.57, -72.61) * mm]});
            skFitSpline(sketch, "E240", {"points": [v(3.57, -72.61) * mm, v(4.07, -71.69) * mm, v(6.12, -71.11) * mm, v(7.53, -71.5) * mm]});
            skFitSpline(sketch, "E241", {"points": [v(7.53, -71.5) * mm, v(8.17, -71.68) * mm, v(8.4, -71.66) * mm, v(8.68, -71.41) * mm]});
            skFitSpline(sketch, "E242", {"points": [v(8.68, -71.41) * mm, v(9.15, -70.98) * mm, v(9.64, -71.02) * mm, v(10.13, -71.54) * mm]});
            skFitSpline(sketch, "E243", {"points": [v(10.13, -71.54) * mm, v(10.44, -71.88) * mm, v(10.95, -72.03) * mm, v(12.2, -72.17) * mm]});
            skFitSpline(sketch, "E244", {"points": [v(12.2, -72.17) * mm, v(13.1, -72.28) * mm, v(14, -72.32) * mm, v(14.17, -72.26) * mm]});
            skFitSpline(sketch, "E245", {"points": [v(14.17, -72.26) * mm, v(14.75, -72.09) * mm, v(15.04, -72.5) * mm, v(15.33, -73.91) * mm]});
            skFitSpline(sketch, "E246", {"points": [v(15.33, -73.91) * mm, v(15.54, -74.89) * mm, v(15.57, -75.53) * mm, v(15.43, -76.04) * mm]});
            skFitSpline(sketch, "E247", {"points": [v(15.43, -76.04) * mm, v(15.14, -77.06) * mm, v(14.45, -77.87) * mm, v(13.85, -77.87) * mm]});
            skFitSpline(sketch, "E248", {"points": [v(13.85, -77.87) * mm, v(13.06, -77.87) * mm, v(13.01, -78.27) * mm, v(13.7, -79) * mm]});
            skFitSpline(sketch, "E249", {"points": [v(13.7, -79) * mm, v(14.06, -79.37) * mm, v(14.38, -79.86) * mm, v(14.43, -80.1) * mm]});
            skFitSpline(sketch, "E250", {"points": [v(14.43, -80.1) * mm, v(14.5, -80.48) * mm, v(14.55, -80.47) * mm, v(15.03, -79.9) * mm]});
            skFitSpline(sketch, "E251", {"points": [v(15.03, -79.9) * mm, v(15.31, -79.57) * mm, v(16.02, -78.83) * mm, v(16.6, -78.28) * mm]});
            skFitSpline(sketch, "E252", {"points": [v(16.6, -78.28) * mm, v(17.64, -77.28) * mm, v(17.65, -77.26) * mm, v(17.4, -76.55) * mm]});
            skFitSpline(sketch, "E253", {"points": [v(17.4, -76.55) * mm, v(17.05, -75.6) * mm, v(17.07, -74.87) * mm, v(17.45, -74.37) * mm]});
            skFitSpline(sketch, "E254", {"points": [v(17.45, -74.37) * mm, v(17.62, -74.14) * mm, v(17.76, -73.7) * mm, v(17.76, -73.4) * mm]});
            skFitSpline(sketch, "E255", {"points": [v(17.76, -73.4) * mm, v(17.77, -72.89) * mm, v(17.86, -72.83) * mm, v(18.88, -72.7) * mm]});
            skFitSpline(sketch, "E256", {"points": [v(18.88, -72.7) * mm, v(19.5, -72.62) * mm, v(20.47, -72.3) * mm, v(21.04, -71.99) * mm]});
            skFitSpline(sketch, "E257", {"points": [v(21.04, -71.99) * mm, v(22.45, -71.22) * mm, v(23.22, -70.08) * mm, v(23.5, -68.35) * mm]});
            skFitSpline(sketch, "E258", {"points": [v(23.5, -68.35) * mm, v(23.9, -65.9) * mm, v(24.16, -65.2) * mm, v(25.1, -63.87) * mm]});
            skFitSpline(sketch, "E259", {"points": [v(25.1, -63.87) * mm, v(26.18, -62.33) * mm, v(26.35, -61.85) * mm, v(26.67, -59.46) * mm]});
            skFitSpline(sketch, "E260", {"points": [v(26.67, -59.46) * mm, v(26.98, -57.13) * mm, v(27.93, -54.18) * mm, v(28.89, -52.58) * mm]});
            skFitSpline(sketch, "E261", {"points": [v(28.89, -52.58) * mm, v(29.3, -51.88) * mm, v(30.25, -50.69) * mm, v(31, -49.93) * mm]});
            skFitSpline(sketch, "E262", {"points": [v(31, -49.93) * mm, v(33.26, -47.61) * mm, v(35.36, -45.01) * mm, v(35.9, -43.88) * mm]});
            skFitSpline(sketch, "E263", {"points": [v(35.9, -43.88) * mm, v(36.17, -43.28) * mm, v(36.49, -42.11) * mm, v(36.6, -41.27) * mm]});
            skFitSpline(sketch, "E264", {"points": [v(36.6, -41.27) * mm, v(36.81, -39.5) * mm, v(37.06, -39.06) * mm, v(38.37, -38.07) * mm]});
            skFitSpline(sketch, "E265", {"points": [v(38.37, -38.07) * mm, v(39.26, -37.4) * mm, v(40.2, -36.1) * mm, v(40.2, -35.57) * mm]});
            skFitSpline(sketch, "E266", {"points": [v(40.2, -35.57) * mm, v(40.2, -35.45) * mm, v(39.98, -35.11) * mm, v(39.7, -34.83) * mm]});
            skFitSpline(sketch, "E267", {"points": [v(39.7, -34.83) * mm, v(38.98, -34.12) * mm, v(38.86, -33.18) * mm, v(39.13, -30.68) * mm]});
            skFitSpline(sketch, "E268", {"points": [v(39.13, -30.68) * mm, v(39.26, -29.5) * mm, v(39.36, -26.93) * mm, v(39.36, -24.95) * mm]});
            skFitSpline(sketch, "E269", {"points": [v(39.36, -24.95) * mm, v(39.36, -21.87) * mm, v(39.3, -21.22) * mm, v(38.94, -20.3) * mm]});
            skFitSpline(sketch, "E270", {"points": [v(38.94, -20.3) * mm, v(38.39, -18.9) * mm, v(38.4, -18.51) * mm, v(39.04, -18) * mm]});
            skFitSpline(sketch, "E271", {"points": [v(39.04, -18) * mm, v(39.45, -17.69) * mm, v(39.57, -17.4) * mm, v(39.57, -16.76) * mm]});
            skFitSpline(sketch, "E272", {"points": [v(39.57, -16.76) * mm, v(39.57, -16.2) * mm, v(39.7, -15.8) * mm, v(39.97, -15.56) * mm]});
            skFitSpline(sketch, "E273", {"points": [v(39.97, -15.56) * mm, v(40.59, -15) * mm, v(40.32, -14.37) * mm, v(39.46, -14.37) * mm]});
            skFitSpline(sketch, "E274", {"points": [v(39.46, -14.37) * mm, v(38.38, -14.37) * mm, v(37.67, -13.4) * mm, v(37.67, -11.9) * mm]});
            skFitSpline(sketch, "E275", {"points": [v(37.67, -11.9) * mm, v(37.67, -10.72) * mm, v(37.93, -9.95) * mm, v(38.44, -9.65) * mm]});
            skFitSpline(sketch, "E276", {"points": [v(38.44, -9.65) * mm, v(39.04, -9.3) * mm, v(38.7, -8.02) * mm, v(38, -8.02) * mm]});
            skFitSpline(sketch, "E277", {"points": [v(38, -8.02) * mm, v(37.74, -8.02) * mm, v(37, -7.64) * mm, v(36.34, -7.18) * mm]});
            skFitSpline(sketch, "E278", {"points": [v(36.34, -7.18) * mm, v(35.18, -6.34) * mm, v(34.43, -6.12) * mm, v(34.18, -6.54) * mm]});
            skFitSpline(sketch, "E279", {"points": [v(34.18, -6.54) * mm, v(34.1, -6.66) * mm, v(33.87, -6.75) * mm, v(33.65, -6.75) * mm]});
            skFitSpline(sketch, "E280", {"points": [v(33.65, -6.75) * mm, v(33.07, -6.75) * mm, v(30.08, -5.09) * mm, v(29.83, -4.63) * mm]});
            skFitSpline(sketch, "E281", {"points": [v(29.83, -4.63) * mm, v(29.5, -4) * mm, v(29.6, -2.89) * mm, v(30.04, -2.22) * mm]});
            skFitSpline(sketch, "E282", {"points": [v(30.04, -2.22) * mm, v(30.4, -1.66) * mm, v(30.41, -1.54) * mm, v(30.14, -1.01) * mm]});
            skFitSpline(sketch, "E283", {"points": [v(30.14, -1.01) * mm, v(29.71, -0.19) * mm, v(29.76, 0.38) * mm, v(30.37, 1.68) * mm]});
            skFitSpline(sketch, "E284", {"points": [v(30.37, 1.68) * mm, v(30.96, 2.95) * mm, v(31, 3.5) * mm, v(30.65, 4.7) * mm]});
            skFitSpline(sketch, "E285", {"points": [v(30.65, 4.7) * mm, v(30.44, 5.4) * mm, v(30.46, 5.58) * mm, v(30.78, 5.93) * mm]});
            skFitSpline(sketch, "E286", {"points": [v(30.78, 5.93) * mm, v(31.13, 6.33) * mm, v(31.13, 6.4) * mm, v(30.68, 7.79) * mm]});
            skFitSpline(sketch, "E287", {"points": [v(30.68, 7.79) * mm, v(30.01, 9.8) * mm, v(29.64, 10.47) * mm, v(28.1, 12.43) * mm]});
            skFitSpline(sketch, "E288", {"points": [v(28.1, 12.43) * mm, v(27.35, 13.37) * mm, v(26.61, 14.44) * mm, v(26.46, 14.8) * mm]});
            skFitSpline(sketch, "E289", {"points": [v(26.46, 14.8) * mm, v(26, 15.95) * mm, v(26.28, 17.5) * mm, v(27.26, 19.16) * mm]});
            skFitSpline(sketch, "E290", {"points": [v(27.26, 19.16) * mm, v(28.4, 21.1) * mm, v(28.53, 21.7) * mm, v(27.93, 22.5) * mm]});
            skFitSpline(sketch, "E291", {"points": [v(27.93, 22.5) * mm, v(27.4, 23.23) * mm, v(27.46, 23.77) * mm, v(28.28, 25.17) * mm]});
            skFitSpline(sketch, "E292", {"points": [v(28.28, 25.17) * mm, v(28.94, 26.3) * mm, v(29.89, 26.9) * mm, v(31.02, 26.9) * mm]});
            skFitSpline(sketch, "E293", {"points": [v(31.02, 26.9) * mm, v(31.6, 26.9) * mm, v(32.1, 27.06) * mm, v(32.48, 27.36) * mm]});
            skFitSpline(sketch, "E294", {"points": [v(32.48, 27.36) * mm, v(33, 27.78) * mm, v(33.05, 27.91) * mm, v(32.96, 28.95) * mm]});
            skFitSpline(sketch, "E295", {"points": [v(32.96, 28.95) * mm, v(32.91, 29.57) * mm, v(32.82, 30.13) * mm, v(32.76, 30.19) * mm]});
            skFitSpline(sketch, "E296", {"points": [v(32.76, 30.19) * mm, v(32.7, 30.25) * mm, v(32.3, 30.15) * mm, v(31.89, 29.97) * mm]});
            skFitSpline(sketch, "E297", {"points": [v(31.89, 29.97) * mm, v(31.46, 29.8) * mm, v(31.06, 29.65) * mm, v(30.98, 29.65) * mm]});
            skFitSpline(sketch, "E298", {"points": [v(30.98, 29.65) * mm, v(30.9, 29.65) * mm, v(30.9, 30.37) * mm, v(30.97, 31.24) * mm]});
            skFitSpline(sketch, "E299", {"points": [v(30.97, 31.24) * mm, v(31.1, 32.73) * mm, v(31.07, 32.83) * mm, v(30.68, 32.83) * mm]});
            skFitSpline(sketch, "E300", {"points": [v(30.68, 32.83) * mm, v(30.45, 32.83) * mm, v(30.26, 32.97) * mm, v(30.26, 33.15) * mm]});
            skFitSpline(sketch, "E301", {"points": [v(30.26, 33.15) * mm, v(30.26, 33.32) * mm, v(30.16, 33.46) * mm, v(30.05, 33.46) * mm]});
            skFitSpline(sketch, "E302", {"points": [v(30.05, 33.46) * mm, v(29.69, 33.46) * mm, v(29.82, 34.44) * mm, v(30.23, 34.81) * mm]});
            skFitSpline(sketch, "E303", {"points": [v(30.23, 34.81) * mm, v(30.44, 35) * mm, v(31.16, 35.28) * mm, v(31.83, 35.42) * mm]});
            skFitSpline(sketch, "E304", {"points": [v(31.83, 35.42) * mm, v(32.85, 35.63) * mm, v(33.13, 35.62) * mm, v(33.6, 35.36) * mm]});
            skFitSpline(sketch, "E305", {"points": [v(33.6, 35.36) * mm, v(34.37, 34.93) * mm, v(34.48, 34.05) * mm, v(33.82, 33.73) * mm]});
            skFitSpline(sketch, "E306", {"points": [v(33.82, 33.73) * mm, v(33.34, 33.51) * mm, v(33.35, 33.5) * mm, v(34.15, 33.16) * mm]});
            skFitSpline(sketch, "E307", {"points": [v(34.15, 33.16) * mm, v(34.9, 32.83) * mm, v(34.99, 32.83) * mm, v(35.36, 33.17) * mm]});
            skFitSpline(sketch, "E308", {"points": [v(35.36, 33.17) * mm, v(35.58, 33.37) * mm, v(35.76, 33.64) * mm, v(35.76, 33.77) * mm]});
            skFitSpline(sketch, "E309", {"points": [v(35.76, 33.77) * mm, v(35.76, 33.9) * mm, v(36.1, 34.7) * mm, v(36.5, 35.56) * mm]});
            skFitSpline(sketch, "E310", {"points": [v(36.5, 35.56) * mm, v(37.29, 37.18) * mm, v(37.3, 37.75) * mm, v(36.61, 38.12) * mm]});
            skFitSpline(sketch, "E311", {"points": [v(36.61, 38.12) * mm, v(36.14, 38.38) * mm, v(35.55, 38.19) * mm, v(35.55, 37.78) * mm]});
            skFitSpline(sketch, "E312", {"points": [v(35.55, 37.78) * mm, v(35.55, 36.66) * mm, v(30.79, 39.12) * mm, v(30.36, 40.45) * mm]});
            skFitSpline(sketch, "E313", {"points": [v(30.36, 40.45) * mm, v(30.3, 40.68) * mm, v(30.34, 41.05) * mm, v(30.47, 41.29) * mm]});
            skFitSpline(sketch, "E314", {"points": [v(30.47, 41.29) * mm, v(30.77, 41.86) * mm, v(31.55, 41.83) * mm, v(33.01, 41.2) * mm]});
            skFitSpline(sketch, "E315", {"points": [v(33.01, 41.2) * mm, v(34.25, 40.67) * mm, v(34.4, 40.66) * mm, v(34.2, 41.18) * mm]});
            skFitSpline(sketch, "E316", {"points": [v(34.2, 41.18) * mm, v(34.13, 41.4) * mm, v(33.81, 41.5) * mm, v(33.34, 41.5) * mm]});
            skFitSpline(sketch, "E317", {"points": [v(33.34, 41.5) * mm, v(32.48, 41.5) * mm, v(32.37, 41.83) * mm, v(32.97, 42.57) * mm]});
            skFitSpline(sketch, "E318", {"points": [v(32.97, 42.57) * mm, v(33.3, 42.96) * mm, v(33.56, 43.04) * mm, v(34.54, 43.04) * mm]});
            skFitSpline(sketch, "E319", {"points": [v(34.54, 43.04) * mm, v(36.05, 43.02) * mm, v(36.12, 43.25) * mm, v(35.4, 45.67) * mm]});
            skFitSpline(sketch, "E320", {"points": [v(35.4, 45.67) * mm, v(34.98, 47.1) * mm, v(34.9, 47.7) * mm, v(35.01, 48.62) * mm]});
            skFitSpline(sketch, "E321", {"points": [v(35.01, 48.62) * mm, v(35.1, 49.37) * mm, v(35.26, 49.76) * mm, v(35.45, 49.76) * mm]});
            skFitSpline(sketch, "E322", {"points": [v(35.45, 49.76) * mm, v(35.79, 49.76) * mm, v(36.46, 48.04) * mm, v(36.81, 46.27) * mm]});
            skFitSpline(sketch, "E323", {"points": [v(36.81, 46.27) * mm, v(37.15, 44.53) * mm, v(37.45, 43.62) * mm, v(37.68, 43.62) * mm]});
            skFitSpline(sketch, "E324", {"points": [v(37.68, 43.62) * mm, v(37.8, 43.62) * mm, v(37.88, 43.84) * mm, v(37.88, 44.1) * mm]});
            skFitSpline(sketch, "E325", {"points": [v(37.88, 44.1) * mm, v(37.88, 44.74) * mm, v(36.88, 48.83) * mm, v(36.6, 49.36) * mm]});
            skFitSpline(sketch, "E326", {"points": [v(36.6, 49.36) * mm, v(36.47, 49.6) * mm, v(36.29, 50.3) * mm, v(36.19, 50.92) * mm]});
            skFitSpline(sketch, "E327", {"points": [v(36.19, 50.92) * mm, v(36.09, 51.54) * mm, v(35.8, 52.48) * mm, v(35.57, 53.01) * mm]});
            skFitSpline(sketch, "E328", {"points": [v(35.57, 53.01) * mm, v(35.31, 53.57) * mm, v(35.13, 54.41) * mm, v(35.13, 55.03) * mm]});
            skFitSpline(sketch, "E329", {"points": [v(35.13, 55.03) * mm, v(35.13, 56.37) * mm, v(34.52, 57.14) * mm, v(33.05, 57.66) * mm]});
            skFitSpline(sketch, "E330", {"points": [v(33.05, 57.66) * mm, v(31.97, 58.05) * mm, v(31.44, 58.5) * mm, v(31.02, 59.34) * mm]});
            skFitSpline(sketch, "E331", {"points": [v(31.02, 59.34) * mm, v(30.64, 60.08) * mm, v(29.4, 60.31) * mm, v(25.6, 60.34) * mm]});
            skFitSpline(sketch, "E332", {"points": [v(25.6, 60.34) * mm, v(21.36, 60.37) * mm, v(20.2, 60.66) * mm, v(19.62, 61.83) * mm]});
            skFitSpline(sketch, "E333", {"points": [v(19.62, 61.83) * mm, v(19.42, 62.24) * mm, v(19.25, 63.05) * mm, v(19.25, 63.63) * mm]});
            skFitSpline(sketch, "E334", {"points": [v(19.25, 63.63) * mm, v(19.24, 64.97) * mm, v(18.71, 66.14) * mm, v(17.39, 67.73) * mm]});
            skFitSpline(sketch, "E335", {"points": [v(17.39, 67.73) * mm, v(15.95, 69.45) * mm, v(15.56, 70.55) * mm, v(15.72, 72.4) * mm]});
            skFitSpline(sketch, "E336", {"points": [v(15.72, 72.4) * mm, v(15.89, 74.42) * mm, v(15.61, 75.26) * mm, v(14.57, 75.97) * mm]});
            skFitSpline(sketch, "E337", {"points": [v(14.57, 75.97) * mm, v(13.8, 76.48) * mm, v(12.94, 77.13) * mm, v(10.52, 78.96) * mm]});
            skFitSpline(sketch, "E338", {"points": [v(10.52, 78.96) * mm, v(9.93, 79.4) * mm, v(9.37, 79.6) * mm, v(8.4, 79.72) * mm]});
            skFitSpline(sketch, "E339", {"points": [v(8.4, 79.72) * mm, v(7.67, 79.8) * mm, v(6.83, 80.05) * mm, v(6.52, 80.27) * mm]});
            skFitSpline(sketch, "E340", {"points": [v(6.52, 80.27) * mm, v(5.73, 80.83) * mm, v(4.99, 80.76) * mm, v(4.18, 80.06) * mm]});
            skFitSpline(sketch, "E341", {"points": [v(4.18, 80.06) * mm, v(3.06, 79.09) * mm, v(2.62, 78.93) * mm, v(1.4, 79.08) * mm]});
            skFitSpline(sketch, "E342", {"points": [v(-1.23, 77.67) * mm, v(-2.35, 76.53) * mm, v(-2.88, 75.8) * mm, v(-3.2, 74.95) * mm]});
            skFitSpline(sketch, "E343", {"points": [v(-3.2, 74.95) * mm, v(-3.44, 74.31) * mm, v(-3.84, 73.58) * mm, v(-4.08, 73.32) * mm]});
            skFitSpline(sketch, "E344", {"points": [v(-4.08, 73.32) * mm, v(-4.6, 72.75) * mm, v(-5.86, 72.28) * mm, v(-7.31, 72.1) * mm]});
            skFitSpline(sketch, "E345", {"points": [v(-7.31, 72.1) * mm, v(-8.5, 71.94) * mm, v(-9.16, 71.58) * mm, v(-9.92, 70.68) * mm]});
            skFitSpline(sketch, "E346", {"points": [v(-9.92, 70.68) * mm, v(-10.62, 69.85) * mm, v(-11.46, 69.45) * mm, v(-12.51, 69.45) * mm]});
            skFitSpline(sketch, "E347", {"points": [v(-13.27, 67.07) * mm, v(-13.12, 64.4) * mm, v(-13.35, 63.34) * mm, v(-14.15, 63) * mm]});
            skFitSpline(sketch, "E348", {"points": [v(-14.15, 63) * mm, v(-14.41, 62.88) * mm, v(-14.68, 62.54) * mm, v(-14.74, 62.25) * mm]});
            skFitSpline(sketch, "E349", {"points": [v(-14.74, 62.25) * mm, v(-14.95, 61.27) * mm, v(-15.22, 60.8) * mm, v(-15.67, 60.66) * mm]});
            skFitSpline(sketch, "E350", {"points": [v(-15.67, 60.66) * mm, v(-16.3, 60.47) * mm, v(-17.15, 61.07) * mm, v(-17.15, 61.71) * mm]});
            skFitSpline(sketch, "E351", {"points": [v(-17.15, 61.71) * mm, v(-17.15, 62.4) * mm, v(-17.57, 62.62) * mm, v(-17.95, 62.12) * mm]});
            skFitSpline(sketch, "E352", {"points": [v(-17.95, 62.12) * mm, v(-18.25, 61.72) * mm, v(-18.24, 60.86) * mm, v(-17.87, 57.55) * mm]});
            skFitSpline(sketch, "E353", {"points": [v(-17.87, 57.55) * mm, v(-17.76, 56.53) * mm, v(-17.83, 56.11) * mm, v(-18.31, 54.9) * mm]});
            skFitSpline(sketch, "E354", {"points": [v(-18.43, 53.1) * mm, v(-18.09, 52.84) * mm, v(-18, 52.61) * mm, v(-18.12, 52.26) * mm]});
            skFitSpline(sketch, "E355", {"points": [v(-18.12, 52.26) * mm, v(-18.35, 51.5) * mm, v(-18.6, 51.29) * mm, v(-19.44, 51.14) * mm]});
            skFitSpline(sketch, "E356", {"points": [v(-19.44, 51.14) * mm, v(-20.16, 51.02) * mm, v(-20.25, 50.92) * mm, v(-20.59, 49.92) * mm]});
            skFitSpline(sketch, "E357", {"points": [v(-20.59, 49.92) * mm, v(-21.07, 48.49) * mm, v(-20.79, 47.82) * mm, v(-19.64, 47.63) * mm]});
            skFitSpline(sketch, "E358", {"points": [v(-19.64, 47.63) * mm, v(-18.7, 47.48) * mm, v(-18.1, 46.98) * mm, v(-17.9, 46.22) * mm]});
            skFitSpline(sketch, "E359", {"points": [v(-17.9, 46.22) * mm, v(-17.82, 45.92) * mm, v(-17.92, 44.77) * mm, v(-18.12, 43.68) * mm]});
            skFitSpline(sketch, "E360", {"points": [v(-18.12, 43.68) * mm, v(-18.44, 41.9) * mm, v(-18.54, 41.66) * mm, v(-19.03, 41.44) * mm]});
            skFitSpline(sketch, "E361", {"points": [v(-19.03, 41.44) * mm, v(-19.33, 41.3) * mm, v(-19.75, 41.02) * mm, v(-19.96, 40.82) * mm]});
            skFitSpline(sketch, "E362", {"points": [v(-19.96, 40.82) * mm, v(-20.16, 40.62) * mm, v(-20.6, 40.45) * mm, v(-20.94, 40.45) * mm]});
            skFitSpline(sketch, "E363", {"points": [v(-21.44, 41.8) * mm, v(-21.32, 43.27) * mm, v(-21.6, 44.43) * mm, v(-22.21, 44.98) * mm]});
            skFitSpline(sketch, "E364", {"points": [v(-22.21, 44.98) * mm, v(-22.54, 45.28) * mm, v(-22.7, 45.3) * mm, v(-23.16, 45.08) * mm]});
            skFitSpline(sketch, "E365", {"points": [v(-23.16, 45.08) * mm, v(-23.48, 44.93) * mm, v(-23.72, 44.65) * mm, v(-23.72, 44.41) * mm]});
            skFitSpline(sketch, "E366", {"points": [v(-23.72, 44.41) * mm, v(-23.72, 44.19) * mm, v(-24.06, 43.69) * mm, v(-24.47, 43.3) * mm]});
            skFitSpline(sketch, "E367", {"points": [v(-24.8, 41.05) * mm, v(-24.28, 39.2) * mm, v(-24.4, 38.43) * mm, v(-25.38, 37) * mm]});
            skFitSpline(sketch, "E368", {"points": [v(-25.38, 37) * mm, v(-26.38, 35.55) * mm, v(-26.52, 35.03) * mm, v(-26.15, 34.3) * mm]});
            skFitSpline(sketch, "E369", {"points": [v(-26.15, 34.3) * mm, v(-25.74, 33.52) * mm, v(-25.75, 32.64) * mm, v(-26.17, 31.34) * mm]});
            skFitSpline(sketch, "E370", {"points": [v(-26.17, 31.34) * mm, v(-26.5, 30.34) * mm, v(-26.5, 30.27) * mm, v(-26.05, 29.35) * mm]});
            skFitSpline(sketch, "E371", {"points": [v(-26.05, 29.35) * mm, v(-25.45, 28.12) * mm, v(-24.64, 27.64) * mm, v(-22.5, 27.27) * mm]});
            skFitSpline(sketch, "E372", {"points": [v(-22.5, 27.27) * mm, v(-21.03, 27.01) * mm, v(-20.71, 27.01) * mm, v(-20.51, 27.25) * mm]});
            skFitSpline(sketch, "E373", {"points": [v(-20.51, 27.25) * mm, v(-20.2, 27.62) * mm, v(-19.6, 27.62) * mm, v(-19.29, 27.24) * mm]});
            skFitSpline(sketch, "E374", {"points": [v(-19.29, 27.24) * mm, v(-18.74, 26.58) * mm, v(-18.77, 25.45) * mm, v(-19.37, 23.93) * mm]});
            skFitSpline(sketch, "E375", {"points": [v(-19.37, 23.93) * mm, v(-19.7, 23.08) * mm, v(-20.07, 22.46) * mm, v(-20.24, 22.46) * mm]});
            skFitSpline(sketch, "E376", {"points": [v(-20.24, 22.46) * mm, v(-20.4, 22.46) * mm, v(-20.54, 22.54) * mm, v(-20.54, 22.65) * mm]});
            skFitSpline(sketch, "E377", {"points": [v(-20.54, 22.65) * mm, v(-20.54, 23.08) * mm, v(-22.27, 25) * mm, v(-22.65, 25) * mm]});
            skFitSpline(sketch, "E378", {"points": [v(-22.65, 25) * mm, v(-23.23, 25) * mm, v(-23.72, 24.2) * mm, v(-23.72, 23.22) * mm]});
            skFitSpline(sketch, "E379", {"points": [v(-23.72, 23.22) * mm, v(-23.72, 22.72) * mm, v(-23.92, 22.04) * mm, v(-24.24, 21.5) * mm]});
            skFitSpline(sketch, "E380", {"points": [v(-24.24, 21.5) * mm, v(-24.66, 20.79) * mm, v(-24.75, 20.34) * mm, v(-24.74, 19.26) * mm]});
            skFitSpline(sketch, "E381", {"points": [v(-24.74, 19.26) * mm, v(-24.72, 18.51) * mm, v(-24.78, 17.69) * mm, v(-24.86, 17.43) * mm]});
            skFitSpline(sketch, "E382", {"points": [v(-24.86, 17.43) * mm, v(-25.08, 16.75) * mm, v(-24.82, 16.1) * mm, v(-24.33, 16.1) * mm]});
            skFitSpline(sketch, "E383", {"points": [v(-24.33, 16.1) * mm, v(-23.36, 16.1) * mm, v(-23.83, 14.55) * mm, v(-24.88, 14.3) * mm]});
            skFitSpline(sketch, "E384", {"points": [v(-24.88, 14.3) * mm, v(-25.3, 14.18) * mm, v(-25.36, 14.09) * mm, v(-25.2, 13.77) * mm]});
            skFitSpline(sketch, "E385", {"points": [v(-25.2, 13.77) * mm, v(-24.96, 13.34) * mm, v(-24.91, 12.23) * mm, v(-25.11, 12.03) * mm]});
            skFitSpline(sketch, "E386", {"points": [v(-25.11, 12.03) * mm, v(-25.18, 11.96) * mm, v(-25.46, 11.98) * mm, v(-25.73, 12.09) * mm]});
            skFitSpline(sketch, "E387", {"points": [v(-25.73, 12.09) * mm, v(-26.03, 12.2) * mm, v(-26.5, 12.18) * mm, v(-26.98, 12.04) * mm]});
            skFitSpline(sketch, "E388", {"points": [v(-26.98, 12.04) * mm, v(-28.78, 11.48) * mm, v(-28.79, 13.48) * mm, v(-26.99, 14.98) * mm]});
            skFitSpline(sketch, "E389", {"points": [v(-26.99, 14.98) * mm, v(-26.47, 15.42) * mm, v(-26.04, 15.92) * mm, v(-26.04, 16.09) * mm]});
            skFitSpline(sketch, "E390", {"points": [v(-26.04, 16.09) * mm, v(-26.04, 16.33) * mm, v(-26.1, 16.35) * mm, v(-26.3, 16.15) * mm]});
            skFitSpline(sketch, "E391", {"points": [v(-26.3, 16.15) * mm, v(-26.76, 15.69) * mm, v(-27.73, 15.86) * mm, v(-28.39, 16.52) * mm]});
            skFitSpline(sketch, "E392", {"points": [v(-28.39, 16.52) * mm, v(-28.98, 17.1) * mm, v(-29, 17.22) * mm, v(-29, 18.97) * mm]});
            skFitSpline(sketch, "E393", {"points": [v(-29, 18.97) * mm, v(-29, 20.63) * mm, v(-29.05, 20.82) * mm, v(-29.43, 20.91) * mm]});
            skFitSpline(sketch, "E394", {"points": [v(-29.43, 20.91) * mm, v(-30.19, 21.11) * mm, v(-29.94, 22.23) * mm, v(-28.69, 24.26) * mm]});
            skFitSpline(sketch, "E395", {"points": [v(-28.69, 24.26) * mm, v(-27.87, 25.58) * mm, v(-28, 27.33) * mm, v(-28.9, 27.33) * mm]});
            skFitSpline(sketch, "E396", {"points": [v(-28.9, 27.33) * mm, v(-29.17, 27.33) * mm, v(-29.7, 27.61) * mm, v(-30.07, 27.96) * mm]});
            skFitSpline(sketch, "E397", {"points": [v(-30.07, 27.96) * mm, v(-30.87, 28.71) * mm, v(-31.12, 28.76) * mm, v(-31.12, 28.14) * mm]});
            skFitSpline(sketch, "E398", {"points": [v(-31.12, 28.14) * mm, v(-31.12, 27.9) * mm, v(-30.7, 27.23) * mm, v(-30.17, 26.67) * mm]});
            skFitSpline(sketch, "E399", {"points": [v(-30.17, 26.67) * mm, v(-29.12, 25.55) * mm, v(-29.07, 25.4) * mm, v(-29.55, 24.9) * mm]});
            skFitSpline(sketch, "E400", {"points": [v(-29.55, 24.9) * mm, v(-30.1, 24.36) * mm, v(-30.96, 24.5) * mm, v(-31.6, 25.23) * mm]});
            skFitSpline(sketch, "E401", {"points": [v(-31.6, 25.23) * mm, v(-32.15, 25.85) * mm, v(-32.25, 25.88) * mm, v(-33.19, 25.74) * mm]});
            skFitSpline(sketch, "E402", {"points": [v(-33.19, 25.74) * mm, v(-34.37, 25.57) * mm, v(-35.26, 25.15) * mm, v(-35.43, 24.68) * mm]});
            skFitSpline(sketch, "E403", {"points": [v(-35.43, 24.68) * mm, v(-35.6, 24.23) * mm, v(-35.14, 24.08) * mm, v(-34.43, 24.35) * mm]});
            skFitSpline(sketch, "E404", {"points": [v(-34.43, 24.35) * mm, v(-34.1, 24.48) * mm, v(-33.54, 24.57) * mm, v(-33.15, 24.57) * mm]});
            skFitSpline(sketch, "E405", {"points": [v(-33.15, 24.57) * mm, v(-32.54, 24.57) * mm, v(-32.46, 24.5) * mm, v(-32.44, 24) * mm]});
            skFitSpline(sketch, "E406", {"points": [v(-32.44, 24) * mm, v(-32.43, 23.67) * mm, v(-32.27, 23.06) * mm, v(-32.1, 22.62) * mm]});
            skFitSpline(sketch, "E407", {"points": [v(-32.1, 22.62) * mm, v(-31.58, 21.42) * mm, v(-31.67, 20.28) * mm, v(-32.4, 18.86) * mm]});
            skFitSpline(sketch, "E408", {"points": [v(-32.4, 18.86) * mm, v(-33.14, 17.4) * mm, v(-33.17, 17.05) * mm, v(-32.63, 16.75) * mm]});
            skFitSpline(sketch, "E409", {"points": [v(-32.63, 16.75) * mm, v(-32.1, 16.47) * mm, v(-31.55, 14.82) * mm, v(-31.55, 13.54) * mm]});
            skFitSpline(sketch, "E410", {"points": [v(-31.55, 13.54) * mm, v(-31.55, 12.77) * mm, v(-31.45, 12.46) * mm, v(-31.11, 12.23) * mm]});
            skFitSpline(sketch, "E411", {"points": [v(-31.11, 12.23) * mm, v(-30.88, 12.06) * mm, v(-30.63, 11.6) * mm, v(-30.56, 11.18) * mm]});
            skFitSpline(sketch, "E412", {"points": [v(-30.56, 11.18) * mm, v(-30.46, 10.56) * mm, v(-30.52, 10.4) * mm, v(-30.91, 10.18) * mm]});
            skFitSpline(sketch, "E413", {"points": [v(-30.91, 10.18) * mm, v(-31.53, 9.85) * mm, v(-32.75, 10.1) * mm, v(-33.03, 10.6) * mm]});
            skFitSpline(sketch, "E414", {"points": [v(-33.03, 10.6) * mm, v(-33.14, 10.82) * mm, v(-33.25, 11.41) * mm, v(-33.26, 11.91) * mm]});
            skFitSpline(sketch, "E415", {"points": [v(-33.26, 11.91) * mm, v(-33.27, 12.53) * mm, v(-33.55, 13.4) * mm, v(-34.16, 14.63) * mm]});
            skFitSpline(sketch, "E416", {"points": [v(-34.16, 14.63) * mm, v(-34.97, 16.28) * mm, v(-35.1, 16.43) * mm, v(-35.72, 16.5) * mm]});
            skFitSpline(sketch, "E417", {"points": [v(-35.72, 16.5) * mm, v(-36.31, 16.55) * mm, v(-36.58, 16.38) * mm, v(-37.73, 15.23) * mm]});
            skFitSpline(sketch, "E418", {"points": [v(-37.73, 15.23) * mm, v(-38.93, 14.04) * mm, v(-39.01, 13.9) * mm, v(-38.59, 13.83) * mm]});
            skFitSpline(sketch, "E419", {"points": [v(-38.59, 13.83) * mm, v(-38.17, 13.76) * mm, v(-38.1, 13.62) * mm, v(-38.11, 12.76) * mm]});
            skFitSpline(sketch, "E420", {"points": [v(-38.11, 12.76) * mm, v(-38.12, 12.21) * mm, v(-38.4, 10.97) * mm, v(-38.75, 9.98) * mm]});
            skFitSpline(sketch, "E421", {"points": [v(-38.75, 9.98) * mm, v(-39.51, 7.8) * mm, v(-39.52, 7.37) * mm, v(-38.83, 5.2) * mm]});
            skFitSpline(sketch, "E422", {"points": [v(-38.83, 5.2) * mm, v(-38.38, 3.8) * mm, v(-38.3, 3.15) * mm, v(-38.32, 1.4) * mm]});
            skFitSpline(sketch, "E423", {"points": [v(-38.32, 1.4) * mm, v(-38.34, 0.23) * mm, v(-38.26, -1.1) * mm, v(-38.13, -1.57) * mm]});
            skFitSpline(sketch, "E424", {"points": [v(-38.13, -1.57) * mm, v(-37.77, -2.92) * mm, v(-37.86, -6.07) * mm, v(-38.34, -8.88) * mm]});
            skFitSpline(sketch, "E425", {"points": [v(-38.34, -8.88) * mm, v(-38.63, -10.58) * mm, v(-38.76, -12.12) * mm, v(-38.71, -13.3) * mm]});
            skFitSpline(sketch, "E426", {"points": [v(-38.71, -13.3) * mm, v(-38.65, -14.92) * mm, v(-38.56, -15.24) * mm, v(-37.96, -16.18) * mm]});
            skFitSpline(sketch, "E427", {"points": [v(-37.41, -20.41) * mm, v(-37.55, -24.06) * mm, v(-37.43, -24.65) * mm, v(-36.22, -26.18) * mm]});
            skFitSpline(sketch, "E428", {"points": [v(-36.22, -26.18) * mm, v(-34.5, -28.36) * mm, v(-33.66, -30.2) * mm, v(-33.66, -31.8) * mm]});
            skFitSpline(sketch, "E429", {"points": [v(-33.66, -31.8) * mm, v(-33.66, -32.5) * mm, v(-33.82, -32.8) * mm, v(-34.62, -33.66) * mm]});
            skFitSpline(sketch, "E430", {"points": [v(-34.62, -33.66) * mm, v(-35.46, -34.56) * mm, v(-35.57, -34.79) * mm, v(-35.57, -35.64) * mm]});
            skFitSpline(sketch, "E431", {"points": [v(-35.57, -35.64) * mm, v(-35.57, -36.85) * mm, v(-35.16, -37.86) * mm, v(-34.2, -38.96) * mm]});
            skFitSpline(sketch, "E432", {"points": [v(-34.2, -38.96) * mm, v(-33.8, -39.44) * mm, v(-33.28, -40.4) * mm, v(-33.04, -41.1) * mm]});
            skFitSpline(sketch, "E433", {"points": [v(-33.04, -41.1) * mm, v(-32.76, -41.93) * mm, v(-32.24, -42.8) * mm, v(-31.56, -43.59) * mm]});
            skFitSpline(sketch, "E434", {"points": [v(-31.56, -43.59) * mm, v(-29.64, -45.8) * mm, v(-29.61, -45.88) * mm, v(-29.6, -49.55) * mm]});
            skFitSpline(sketch, "E435", {"points": [v(-29.6, -49.55) * mm, v(-29.59, -51.33) * mm, v(-29.65, -53.1) * mm, v(-29.74, -53.47) * mm]});
            skFitSpline(sketch, "E436", {"points": [v(-29.74, -53.47) * mm, v(-29.87, -54.05) * mm, v(-29.78, -54.34) * mm, v(-29.2, -55.24) * mm]});
            skFitSpline(sketch, "E437", {"points": [v(-29.2, -55.24) * mm, v(-28.02, -57.1) * mm, v(-28.34, -58.63) * mm, v(-30.4, -60.92) * mm]});
            skFitSpline(sketch, "E438", {"points": [v(-30.9, -63.02) * mm, v(-30.62, -63.56) * mm, v(-29.54, -65.09) * mm, v(-28.5, -66.4) * mm]});
            skFitSpline(sketch, "E439", {"points": [v(-28.5, -66.4) * mm, v(-27.47, -67.73) * mm, v(-25.87, -70.02) * mm, v(-24.93, -71.5) * mm]});
            skFitSpline(sketch, "E440", {"points": [v(-24.93, -71.5) * mm, v(-21.66, -76.64) * mm, v(-20.53, -77.82) * mm, v(-18.3, -78.38) * mm]});
            skFitSpline(sketch, "E441", {"points": [v(-18.3, -78.38) * mm, v(-17.5, -78.58) * mm, v(-15.88, -79.13) * mm, v(-14.72, -79.6) * mm]});
            skFitSpline(sketch, "E442", {"points": [v(-14.72, -79.6) * mm, v(-13.56, -80.07) * mm, v(-12.22, -80.53) * mm, v(-11.76, -80.63) * mm]});
            skFitSpline(sketch, "E443", {"points": [v(-11.76, -80.63) * mm, v(-10.67, -80.86) * mm, v(-8.14, -80.7) * mm, v(-6.84, -80.3) * mm]});
            skFitSpline(sketch, "E444", {"points": [v(-34.5, 19.17) * mm, v(-34.65, 19.34) * mm, v(-35.11, 19.55) * mm, v(-35.54, 19.62) * mm]});
            skFitSpline(sketch, "E445", {"points": [v(-35.54, 19.62) * mm, v(-35.99, 19.7) * mm, v(-36.79, 20.15) * mm, v(-37.44, 20.68) * mm]});
            skFitSpline(sketch, "E446", {"points": [v(-37.44, 20.68) * mm, v(-38.07, 21.2) * mm, v(-38.96, 21.72) * mm, v(-39.42, 21.86) * mm]});
            skFitSpline(sketch, "E447", {"points": [v(-39.42, 21.86) * mm, v(-39.89, 22) * mm, v(-40.41, 22.34) * mm, v(-40.6, 22.6) * mm]});
            skFitSpline(sketch, "E448", {"points": [v(-40.6, 22.6) * mm, v(-40.88, 23.06) * mm, v(-40.88, 23.2) * mm, v(-40.52, 24.1) * mm]});
            skFitSpline(sketch, "E449", {"points": [v(-40.52, 24.1) * mm, v(-39.98, 25.46) * mm, v(-39.97, 28.27) * mm, v(-40.5, 29.07) * mm]});
            skFitSpline(sketch, "E450", {"points": [v(-40.5, 29.07) * mm, v(-40.94, 29.76) * mm, v(-40.96, 30.33) * mm, v(-40.55, 31.12) * mm]});
            skFitSpline(sketch, "E451", {"points": [v(-40.55, 31.12) * mm, v(-40.35, 31.5) * mm, v(-40.29, 32) * mm, v(-40.37, 32.52) * mm]});
            skFitSpline(sketch, "E452", {"points": [v(-40.37, 32.52) * mm, v(-40.49, 33.2) * mm, v(-40.43, 33.39) * mm, v(-39.97, 33.76) * mm]});
            skFitSpline(sketch, "E453", {"points": [v(-39.97, 33.76) * mm, v(-39.45, 34.2) * mm, v(-38.12, 36.16) * mm, v(-37.84, 36.9) * mm]});
            skFitSpline(sketch, "E454", {"points": [v(-37.84, 36.9) * mm, v(-37.74, 37.17) * mm, v(-37.47, 37.27) * mm, v(-36.87, 37.27) * mm]});
            skFitSpline(sketch, "E455", {"points": [v(-36.87, 37.27) * mm, v(-36.4, 37.27) * mm, v(-35.93, 37.4) * mm, v(-35.78, 37.6) * mm]});
            skFitSpline(sketch, "E456", {"points": [v(-35.78, 37.6) * mm, v(-35.64, 37.77) * mm, v(-35.2, 37.9) * mm, v(-34.82, 37.9) * mm]});
            skFitSpline(sketch, "E457", {"points": [v(-34.82, 37.9) * mm, v(-34.13, 37.9) * mm, v(-34.12, 37.9) * mm, v(-34.23, 37.12) * mm]});
            skFitSpline(sketch, "E458", {"points": [v(-34.23, 37.12) * mm, v(-34.47, 35.46) * mm, v(-34.75, 34.75) * mm, v(-35.37, 34.23) * mm]});
            skFitSpline(sketch, "E459", {"points": [v(-35.37, 34.23) * mm, v(-35.99, 33.7) * mm, v(-36, 33.67) * mm, v(-35.67, 33.16) * mm]});
            skFitSpline(sketch, "E460", {"points": [v(-35.67, 33.16) * mm, v(-34.87, 31.95) * mm, v(-36.1, 31.14) * mm, v(-37.5, 31.95) * mm]});
            skFitSpline(sketch, "E461", {"points": [v(-37.5, 31.95) * mm, v(-37.94, 32.2) * mm, v(-38.35, 32.4) * mm, v(-38.4, 32.4) * mm]});
            skFitSpline(sketch, "E462", {"points": [v(-38.4, 32.4) * mm, v(-38.63, 32.4) * mm, v(-38.23, 31.65) * mm, v(-37.44, 30.52) * mm]});
            skFitSpline(sketch, "E463", {"points": [v(-37.44, 30.52) * mm, v(-36.44, 29.1) * mm, v(-36.35, 28.09) * mm, v(-37.16, 27.33) * mm]});
            skFitSpline(sketch, "E464", {"points": [v(-37.16, 27.33) * mm, v(-37.75, 26.77) * mm, v(-37.88, 25.84) * mm, v(-37.36, 25.84) * mm]});
            skFitSpline(sketch, "E465", {"points": [v(-37.36, 25.84) * mm, v(-37.12, 25.84) * mm, v(-37.08, 25.7) * mm, v(-37.18, 25.26) * mm]});
            skFitSpline(sketch, "E466", {"points": [v(-37.18, 25.26) * mm, v(-37.37, 24.47) * mm, v(-37.66, 23.94) * mm, v(-37.9, 23.94) * mm]});
            skFitSpline(sketch, "E467", {"points": [v(-37.9, 23.94) * mm, v(-38.25, 23.94) * mm, v(-38.13, 23.18) * mm, v(-37.73, 22.82) * mm]});
            skFitSpline(sketch, "E468", {"points": [v(-37.73, 22.82) * mm, v(-37.52, 22.63) * mm, v(-36.88, 22.27) * mm, v(-36.3, 22.02) * mm]});
            skFitSpline(sketch, "E469", {"points": [v(-36.3, 22.02) * mm, v(-33.61, 20.87) * mm, v(-33.45, 20.76) * mm, v(-33.45, 20.13) * mm]});
            skFitSpline(sketch, "E470", {"points": [v(-33.45, 20.13) * mm, v(-33.45, 18.94) * mm, v(-33.94, 18.5) * mm, v(-34.5, 19.17) * mm]});
            skFitSpline(sketch, "E471", {"points": [v(-33.88, 20.11) * mm, v(-33.88, 20.2) * mm, v(-34.7, 20.65) * mm, v(-35.7, 21.1) * mm]});
            skFitSpline(sketch, "E472", {"points": [v(-35.7, 21.1) * mm, v(-38.2, 22.21) * mm, v(-38.53, 22.5) * mm, v(-38.53, 23.53) * mm]});
            skFitSpline(sketch, "E473", {"points": [v(-38.53, 23.53) * mm, v(-38.53, 23.99) * mm, v(-38.45, 24.36) * mm, v(-38.35, 24.36) * mm]});
            skFitSpline(sketch, "E474", {"points": [v(-38.35, 24.36) * mm, v(-38.26, 24.36) * mm, v(-38.08, 24.58) * mm, v(-37.96, 24.84) * mm]});
            skFitSpline(sketch, "E475", {"points": [v(-37.96, 24.84) * mm, v(-37.8, 25.2) * mm, v(-37.81, 25.39) * mm, v(-38.03, 25.6) * mm]});
            skFitSpline(sketch, "E476", {"points": [v(-38.03, 25.6) * mm, v(-38.5, 26.03) * mm, v(-38.36, 26.84) * mm, v(-37.67, 27.63) * mm]});
            skFitSpline(sketch, "E477", {"points": [v(-37.67, 27.63) * mm, v(-36.9, 28.51) * mm, v(-36.94, 28.8) * mm, v(-38.14, 30.48) * mm]});
            skFitSpline(sketch, "E478", {"points": [v(-38.14, 30.48) * mm, v(-38.63, 31.17) * mm, v(-38.96, 31.87) * mm, v(-38.96, 32.23) * mm]});
            skFitSpline(sketch, "E479", {"points": [v(-38.96, 32.23) * mm, v(-38.96, 32.75) * mm, v(-38.87, 32.83) * mm, v(-38.36, 32.83) * mm]});
            skFitSpline(sketch, "E480", {"points": [v(-38.36, 32.83) * mm, v(-38.03, 32.83) * mm, v(-37.58, 32.69) * mm, v(-37.36, 32.52) * mm]});
            skFitSpline(sketch, "E481", {"points": [v(-37.36, 32.52) * mm, v(-36.98, 32.23) * mm, v(-36, 32.07) * mm, v(-36, 32.3) * mm]});
            skFitSpline(sketch, "E482", {"points": [v(-36, 32.3) * mm, v(-36, 32.35) * mm, v(-36.15, 32.73) * mm, v(-36.35, 33.14) * mm]});
            skFitSpline(sketch, "E483", {"points": [v(-35.92, 34.57) * mm, v(-35.27, 35.14) * mm, v(-35.1, 35.46) * mm, v(-34.96, 36.38) * mm]});
            skFitSpline(sketch, "E484", {"points": [v(-34.96, 36.38) * mm, v(-34.86, 36.99) * mm, v(-34.82, 37.49) * mm, v(-34.87, 37.49) * mm]});
            skFitSpline(sketch, "E485", {"points": [v(-34.87, 37.49) * mm, v(-34.91, 37.49) * mm, v(-35.23, 37.28) * mm, v(-35.56, 37.04) * mm]});
            skFitSpline(sketch, "E486", {"points": [v(-35.56, 37.04) * mm, v(-35.96, 36.74) * mm, v(-36.36, 36.62) * mm, v(-36.72, 36.69) * mm]});
            skFitSpline(sketch, "E487", {"points": [v(-36.72, 36.69) * mm, v(-37.02, 36.75) * mm, v(-37.26, 36.72) * mm, v(-37.26, 36.64) * mm]});
            skFitSpline(sketch, "E488", {"points": [v(-37.26, 36.64) * mm, v(-37.26, 36.35) * mm, v(-39.4, 33.25) * mm, v(-39.6, 33.25) * mm]});
            skFitSpline(sketch, "E489", {"points": [v(-39.6, 33.25) * mm, v(-39.71, 33.25) * mm, v(-39.8, 32.75) * mm, v(-39.8, 32.14) * mm]});
            skFitSpline(sketch, "E490", {"points": [v(-39.8, 32.14) * mm, v(-39.81, 31.5) * mm, v(-39.95, 30.86) * mm, v(-40.13, 30.62) * mm]});
            skFitSpline(sketch, "E491", {"points": [v(-40.13, 30.62) * mm, v(-40.4, 30.26) * mm, v(-40.4, 30.15) * mm, v(-40.08, 29.67) * mm]});
            skFitSpline(sketch, "E492", {"points": [v(-40.08, 29.67) * mm, v(-39.54, 28.86) * mm, v(-39.43, 25.58) * mm, v(-39.9, 24.18) * mm]});
            skFitSpline(sketch, "E493", {"points": [v(-39.9, 24.18) * mm, v(-40.1, 23.59) * mm, v(-40.2, 23.02) * mm, v(-40.14, 22.92) * mm]});
            skFitSpline(sketch, "E494", {"points": [v(-40.14, 22.92) * mm, v(-40.08, 22.82) * mm, v(-39.57, 22.56) * mm, v(-39.02, 22.35) * mm]});
            skFitSpline(sketch, "E495", {"points": [v(-39.02, 22.35) * mm, v(-38.46, 22.15) * mm, v(-37.5, 21.56) * mm, v(-36.87, 21.05) * mm]});
            skFitSpline(sketch, "E496", {"points": [v(-36.87, 21.05) * mm, v(-36.12, 20.45) * mm, v(-35.53, 20.13) * mm, v(-35.13, 20.13) * mm]});
            skFitSpline(sketch, "E497", {"points": [v(-35.13, 20.13) * mm, v(-34.8, 20.13) * mm, v(-34.48, 20.03) * mm, v(-34.4, 19.91) * mm]});
            skFitSpline(sketch, "E498", {"points": [v(-34.4, 19.91) * mm, v(-34.26, 19.68) * mm, v(-33.88, 19.83) * mm, v(-33.88, 20.11) * mm]});
            skFitSpline(sketch, "E499", {"points": [v(-35.84, 27.25) * mm, v(-35.9, 27.35) * mm, v(-36.01, 27.96) * mm, v(-36.1, 28.6) * mm]});
            skFitSpline(sketch, "E500", {"points": [v(-36.1, 28.6) * mm, v(-36.27, 30.1) * mm, v(-35.9, 30.72) * mm, v(-35.07, 30.34) * mm]});
            skFitSpline(sketch, "E501", {"points": [v(-35.07, 30.34) * mm, v(-34.7, 30.18) * mm, v(-34.56, 29.98) * mm, v(-34.64, 29.77) * mm]});
            skFitSpline(sketch, "E502", {"points": [v(-34.64, 29.77) * mm, v(-34.74, 29.52) * mm, v(-34.61, 29.44) * mm, v(-34.1, 29.44) * mm]});
            skFitSpline(sketch, "E503", {"points": [v(-34.1, 29.44) * mm, v(-33.14, 29.44) * mm, v(-32.6, 29.1) * mm, v(-32.6, 28.48) * mm]});
            skFitSpline(sketch, "E504", {"points": [v(-32.6, 28.48) * mm, v(-32.6, 28.2) * mm, v(-32.71, 27.96) * mm, v(-32.85, 27.96) * mm]});
            skFitSpline(sketch, "E505", {"points": [v(-32.85, 27.96) * mm, v(-32.98, 27.96) * mm, v(-33.2, 27.8) * mm, v(-33.34, 27.62) * mm]});
            skFitSpline(sketch, "E506", {"points": [v(-33.34, 27.62) * mm, v(-33.62, 27.24) * mm, v(-35.65, 26.94) * mm, v(-35.84, 27.25) * mm]});
            skFitSpline(sketch, "E507", {"points": [v(-33.88, 28.07) * mm, v(-33.88, 28.24) * mm, v(-33.73, 28.38) * mm, v(-33.56, 28.38) * mm]});
            skFitSpline(sketch, "E508", {"points": [v(-33.56, 28.38) * mm, v(-33.38, 28.38) * mm, v(-33.24, 28.48) * mm, v(-33.24, 28.6) * mm]});
            skFitSpline(sketch, "E509", {"points": [v(-33.24, 28.6) * mm, v(-33.24, 28.71) * mm, v(-33.73, 28.8) * mm, v(-34.32, 28.8) * mm]});
            skFitSpline(sketch, "E510", {"points": [v(-34.32, 28.8) * mm, v(-35.4, 28.8) * mm, v(-35.4, 28.81) * mm, v(-35.31, 29.43) * mm]});
            skFitSpline(sketch, "E511", {"points": [v(-35.31, 29.43) * mm, v(-35.26, 29.77) * mm, v(-35.3, 30) * mm, v(-35.4, 29.95) * mm]});
            skFitSpline(sketch, "E512", {"points": [v(-35.4, 29.95) * mm, v(-35.6, 29.82) * mm, v(-35.62, 28.91) * mm, v(-35.44, 28.23) * mm]});
            skFitSpline(sketch, "E513", {"points": [v(-35.44, 28.23) * mm, v(-35.33, 27.85) * mm, v(-35.16, 27.75) * mm, v(-34.6, 27.75) * mm]});
            skFitSpline(sketch, "E514", {"points": [v(-34.6, 27.75) * mm, v(-34.1, 27.75) * mm, v(-33.88, 27.85) * mm, v(-33.88, 28.07) * mm]});
            skFitSpline(sketch, "E515", {"points": [v(-34.5, 30.49) * mm, v(-34.87, 31.18) * mm, v(-34.75, 31.97) * mm, v(-34.2, 32.53) * mm]});
            skFitSpline(sketch, "E516", {"points": [v(-34.2, 32.53) * mm, v(-33.9, 32.82) * mm, v(-33.66, 33.2) * mm, v(-33.66, 33.37) * mm]});
            skFitSpline(sketch, "E517", {"points": [v(-33.66, 33.37) * mm, v(-33.66, 33.54) * mm, v(-33.57, 33.68) * mm, v(-33.45, 33.68) * mm]});
            skFitSpline(sketch, "E518", {"points": [v(-33.45, 33.68) * mm, v(-33.34, 33.68) * mm, v(-33.24, 33.6) * mm, v(-33.24, 33.51) * mm]});
            skFitSpline(sketch, "E519", {"points": [v(-33.24, 33.51) * mm, v(-33.24, 33.42) * mm, v(-32.95, 33.24) * mm, v(-32.6, 33.1) * mm]});
            skFitSpline(sketch, "E520", {"points": [v(-32.6, 33.1) * mm, v(-31.72, 32.77) * mm, v(-31.8, 32.27) * mm, v(-32.94, 31.08) * mm]});
            skFitSpline(sketch, "E521", {"points": [v(-32.94, 31.08) * mm, v(-34, 29.96) * mm, v(-34.19, 29.9) * mm, v(-34.5, 30.49) * mm]});
            skFitSpline(sketch, "E522", {"points": [v(-32.6, 32.45) * mm, v(-32.6, 32.54) * mm, v(-32.75, 32.62) * mm, v(-32.92, 32.62) * mm]});
            skFitSpline(sketch, "E523", {"points": [v(-32.92, 32.62) * mm, v(-33.1, 32.62) * mm, v(-33.24, 32.53) * mm, v(-33.24, 32.43) * mm]});
            skFitSpline(sketch, "E524", {"points": [v(-33.24, 32.43) * mm, v(-33.24, 32.33) * mm, v(-33.43, 32.2) * mm, v(-33.66, 32.13) * mm]});
            skFitSpline(sketch, "E525", {"points": [v(-33.66, 32.13) * mm, v(-33.96, 32.06) * mm, v(-34.09, 31.84) * mm, v(-34.09, 31.43) * mm]});
            skFitSpline(sketch, "E526", {"points": [v(-33.35, 31.56) * mm, v(-32.94, 31.95) * mm, v(-32.6, 32.35) * mm, v(-32.6, 32.45) * mm]});
            skSolve(sketch);
        }
        {
            var Q0;
            Q0=makeQuery(id+"F0.imprint","IMPRINT",FACE,{"disambiguationData":[TD([[makeQuery(id+"F0.imprint","IMPRINT",EDGE,{"derivedFrom":sQuery(id+"F0.wireOp",EDGE,"E0.bottom")}),-1.0]])]});
            extrude(context, id + "F1", {"entities" : qUnion([Q0]), "depth" : 3 * mm, "offsetDistance" : 25 * mm});
        }
        {
            var Q0;
            Q0=makeQuery(id+"F1.opExtrude","CAP_FACE",FACE,{"disambiguationData":[OSD([sQuery(id+"F0.wireOp",EDGE,"E0.bottom"),sQuery(id+"F0.wireOp",EDGE,"E0.top"),sQuery(id+"F0.wireOp",EDGE,"E0.left"),sQuery(id+"F0.wireOp",EDGE,"E0.right"),sQuery(id+"F0.wireOp",EDGE,"E1"),sQuery(id+"F0.wireOp",EDGE,"E2"),sQuery(id+"F0.wireOp",EDGE,"E3"),sQuery(id+"F0.wireOp",EDGE,"E4"),sQuery(id+"F0.wireOp",EDGE,"E5"),sQuery(id+"F0.wireOp",EDGE,"E6"),sQuery(id+"F0.wireOp",EDGE,"E7"),sQuery(id+"F0.wireOp",EDGE,"E8"),sQuery(id+"F0.wireOp",EDGE,"E9"),sQuery(id+"F0.wireOp",EDGE,"E10"),sQuery(id+"F0.wireOp",EDGE,"E11"),sQuery(id+"F0.wireOp",EDGE,"E12"),sQuery(id+"F0.wireOp",EDGE,"E31"),sQuery(id+"F0.wireOp",EDGE,"E32"),sQuery(id+"F0.wireOp",EDGE,"E33"),sQuery(id+"F0.wireOp",EDGE,"E34"),sQuery(id+"F0.wireOp",EDGE,"E35"),sQuery(id+"F0.wireOp",EDGE,"E36"),sQuery(id+"F0.wireOp",EDGE,"E37"),sQuery(id+"F0.wireOp",EDGE,"E38"),sQuery(id+"F0.wireOp",EDGE,"E39"),sQuery(id+"F0.wireOp",EDGE,"E40"),sQuery(id+"F0.wireOp",EDGE,"E41"),sQuery(id+"F0.wireOp",EDGE,"E42"),sQuery(id+"F0.wireOp",EDGE,"E43"),sQuery(id+"F0.wireOp",EDGE,"E44"),sQuery(id+"F0.wireOp",EDGE,"E45"),sQuery(id+"F0.wireOp",EDGE,"E46"),sQuery(id+"F0.wireOp",EDGE,"E47"),sQuery(id+"F0.wireOp",EDGE,"E48"),sQuery(id+"F0.wireOp",EDGE,"E49"),sQuery(id+"F0.wireOp",EDGE,"E50"),sQuery(id+"F0.wireOp",EDGE,"E51"),sQuery(id+"F0.wireOp",EDGE,"E52"),sQuery(id+"F0.wireOp",EDGE,"E53"),sQuery(id+"F0.wireOp",EDGE,"E54"),sQuery(id+"F0.wireOp",EDGE,"E55"),sQuery(id+"F0.wireOp",EDGE,"E56"),sQuery(id+"F0.wireOp",EDGE,"E57"),sQuery(id+"F0.wireOp",EDGE,"E58"),sQuery(id+"F0.wireOp",EDGE,"E59"),sQuery(id+"F0.wireOp",EDGE,"E60"),sQuery(id+"F0.wireOp",EDGE,"E61"),sQuery(id+"F0.wireOp",EDGE,"E62"),sQuery(id+"F0.wireOp",EDGE,"E63"),sQuery(id+"F0.wireOp",EDGE,"E64"),sQuery(id+"F0.wireOp",EDGE,"E65"),sQuery(id+"F0.wireOp",EDGE,"E66"),sQuery(id+"F0.wireOp",EDGE,"E67"),sQuery(id+"F0.wireOp",EDGE,"E68"),sQuery(id+"F0.wireOp",EDGE,"E69"),sQuery(id+"F0.wireOp",EDGE,"E70"),sQuery(id+"F0.wireOp",EDGE,"E71"),sQuery(id+"F0.wireOp",EDGE,"E72"),sQuery(id+"F0.wireOp",EDGE,"E73"),sQuery(id+"F0.wireOp",EDGE,"E74"),sQuery(id+"F0.wireOp",EDGE,"E75"),sQuery(id+"F0.wireOp",EDGE,"E76"),sQuery(id+"F0.wireOp",EDGE,"E77"),sQuery(id+"F0.wireOp",EDGE,"E78"),sQuery(id+"F0.wireOp",EDGE,"E79"),sQuery(id+"F0.wireOp",EDGE,"E80"),sQuery(id+"F0.wireOp",EDGE,"E81"),sQuery(id+"F0.wireOp",EDGE,"E82"),sQuery(id+"F0.wireOp",EDGE,"E83"),sQuery(id+"F0.wireOp",EDGE,"E84"),sQuery(id+"F0.wireOp",EDGE,"E85"),sQuery(id+"F0.wireOp",EDGE,"E86"),sQuery(id+"F0.wireOp",EDGE,"E87"),sQuery(id+"F0.wireOp",EDGE,"E88"),sQuery(id+"F0.wireOp",EDGE,"E89"),sQuery(id+"F0.wireOp",EDGE,"E90"),sQuery(id+"F0.wireOp",EDGE,"E91"),sQuery(id+"F0.wireOp",EDGE,"E92"),sQuery(id+"F0.wireOp",EDGE,"E93"),sQuery(id+"F0.wireOp",EDGE,"E94"),sQuery(id+"F0.wireOp",EDGE,"E95"),sQuery(id+"F0.wireOp",EDGE,"E96"),sQuery(id+"F0.wireOp",EDGE,"E97"),sQuery(id+"F0.wireOp",EDGE,"E98"),sQuery(id+"F0.wireOp",EDGE,"E99"),sQuery(id+"F0.wireOp",EDGE,"E100"),sQuery(id+"F0.wireOp",EDGE,"E101"),sQuery(id+"F0.wireOp",EDGE,"E102"),sQuery(id+"F0.wireOp",EDGE,"E103"),sQuery(id+"F0.wireOp",EDGE,"E104"),sQuery(id+"F0.wireOp",EDGE,"E105"),sQuery(id+"F0.wireOp",EDGE,"E106"),sQuery(id+"F0.wireOp",EDGE,"E107"),sQuery(id+"F0.wireOp",EDGE,"E108"),sQuery(id+"F0.wireOp",EDGE,"E109"),sQuery(id+"F0.wireOp",EDGE,"E110"),sQuery(id+"F0.wireOp",EDGE,"E111"),sQuery(id+"F0.wireOp",EDGE,"E112"),sQuery(id+"F0.wireOp",EDGE,"E113"),sQuery(id+"F0.wireOp",EDGE,"E114"),sQuery(id+"F0.wireOp",EDGE,"E115"),sQuery(id+"F0.wireOp",EDGE,"E116"),sQuery(id+"F0.wireOp",EDGE,"E117"),sQuery(id+"F0.wireOp",EDGE,"E118"),sQuery(id+"F0.wireOp",EDGE,"E119"),sQuery(id+"F0.wireOp",EDGE,"E120"),sQuery(id+"F0.wireOp",EDGE,"E121"),sQuery(id+"F0.wireOp",EDGE,"E122"),sQuery(id+"F0.wireOp",EDGE,"E123"),sQuery(id+"F0.wireOp",EDGE,"E124"),sQuery(id+"F0.wireOp",EDGE,"E125"),sQuery(id+"F0.wireOp",EDGE,"E126"),sQuery(id+"F0.wireOp",EDGE,"E127"),sQuery(id+"F0.wireOp",EDGE,"E128"),sQuery(id+"F0.wireOp",EDGE,"E129"),sQuery(id+"F0.wireOp",EDGE,"E130"),sQuery(id+"F0.wireOp",EDGE,"E131"),sQuery(id+"F0.wireOp",EDGE,"E132"),sQuery(id+"F0.wireOp",EDGE,"E133"),sQuery(id+"F0.wireOp",EDGE,"E134"),sQuery(id+"F0.wireOp",EDGE,"E135"),sQuery(id+"F0.wireOp",EDGE,"E136"),sQuery(id+"F0.wireOp",EDGE,"E137"),sQuery(id+"F0.wireOp",EDGE,"E138"),sQuery(id+"F0.wireOp",EDGE,"E139"),sQuery(id+"F0.wireOp",EDGE,"E140"),sQuery(id+"F0.wireOp",EDGE,"E141"),sQuery(id+"F0.wireOp",EDGE,"E142"),sQuery(id+"F0.wireOp",EDGE,"E143"),sQuery(id+"F0.wireOp",EDGE,"E144"),sQuery(id+"F0.wireOp",EDGE,"E145"),sQuery(id+"F0.wireOp",EDGE,"E146"),sQuery(id+"F0.wireOp",EDGE,"E147"),sQuery(id+"F0.wireOp",EDGE,"E148"),sQuery(id+"F0.wireOp",EDGE,"E149"),sQuery(id+"F0.wireOp",EDGE,"E150"),sQuery(id+"F0.wireOp",EDGE,"E151"),sQuery(id+"F0.wireOp",EDGE,"E152"),sQuery(id+"F0.wireOp",EDGE,"E153"),sQuery(id+"F0.wireOp",EDGE,"E154"),sQuery(id+"F0.wireOp",EDGE,"E155"),sQuery(id+"F0.wireOp",EDGE,"E156"),sQuery(id+"F0.wireOp",EDGE,"E157"),sQuery(id+"F0.wireOp",EDGE,"E158"),sQuery(id+"F0.wireOp",EDGE,"E159"),sQuery(id+"F0.wireOp",EDGE,"E160"),sQuery(id+"F0.wireOp",EDGE,"E161"),sQuery(id+"F0.wireOp",EDGE,"E162"),sQuery(id+"F0.wireOp",EDGE,"E163"),sQuery(id+"F0.wireOp",EDGE,"E164"),sQuery(id+"F0.wireOp",EDGE,"E165"),sQuery(id+"F0.wireOp",EDGE,"E166"),sQuery(id+"F0.wireOp",EDGE,"E167"),sQuery(id+"F0.wireOp",EDGE,"E168"),sQuery(id+"F0.wireOp",EDGE,"E169"),sQuery(id+"F0.wireOp",EDGE,"E170"),sQuery(id+"F0.wireOp",EDGE,"E171"),sQuery(id+"F0.wireOp",EDGE,"E172"),sQuery(id+"F0.wireOp",EDGE,"E173"),sQuery(id+"F0.wireOp",EDGE,"E174"),sQuery(id+"F0.wireOp",EDGE,"E175"),sQuery(id+"F0.wireOp",EDGE,"E176"),sQuery(id+"F0.wireOp",EDGE,"E177"),sQuery(id+"F0.wireOp",EDGE,"E178"),sQuery(id+"F0.wireOp",EDGE,"E179"),sQuery(id+"F0.wireOp",EDGE,"E180"),sQuery(id+"F0.wireOp",EDGE,"E181"),sQuery(id+"F0.wireOp",EDGE,"E182"),sQuery(id+"F0.wireOp",EDGE,"E183"),sQuery(id+"F0.wireOp",EDGE,"E184"),sQuery(id+"F0.wireOp",EDGE,"E185"),sQuery(id+"F0.wireOp",EDGE,"E186"),sQuery(id+"F0.wireOp",EDGE,"E187"),sQuery(id+"F0.wireOp",EDGE,"E188"),sQuery(id+"F0.wireOp",EDGE,"E189"),sQuery(id+"F0.wireOp",EDGE,"E190"),sQuery(id+"F0.wireOp",EDGE,"E191"),sQuery(id+"F0.wireOp",EDGE,"E192"),sQuery(id+"F0.wireOp",EDGE,"E193"),sQuery(id+"F0.wireOp",EDGE,"E194"),sQuery(id+"F0.wireOp",EDGE,"E195"),sQuery(id+"F0.wireOp",EDGE,"E196"),sQuery(id+"F0.wireOp",EDGE,"E197"),sQuery(id+"F0.wireOp",EDGE,"E198"),sQuery(id+"F0.wireOp",EDGE,"E199"),sQuery(id+"F0.wireOp",EDGE,"E200"),sQuery(id+"F0.wireOp",EDGE,"E201"),sQuery(id+"F0.wireOp",EDGE,"E202"),sQuery(id+"F0.wireOp",EDGE,"E203"),sQuery(id+"F0.wireOp",EDGE,"E204"),sQuery(id+"F0.wireOp",EDGE,"E205"),sQuery(id+"F0.wireOp",EDGE,"E206"),sQuery(id+"F0.wireOp",EDGE,"E207"),sQuery(id+"F0.wireOp",EDGE,"E208"),sQuery(id+"F0.wireOp",EDGE,"E209"),sQuery(id+"F0.wireOp",EDGE,"E210"),sQuery(id+"F0.wireOp",EDGE,"E211"),sQuery(id+"F0.wireOp",EDGE,"E212"),sQuery(id+"F0.wireOp",EDGE,"E213"),sQuery(id+"F0.wireOp",EDGE,"E214"),sQuery(id+"F0.wireOp",EDGE,"E215"),sQuery(id+"F0.wireOp",EDGE,"E216"),sQuery(id+"F0.wireOp",EDGE,"E217"),sQuery(id+"F0.wireOp",EDGE,"E218"),sQuery(id+"F0.wireOp",EDGE,"E219"),sQuery(id+"F0.wireOp",EDGE,"E220"),sQuery(id+"F0.wireOp",EDGE,"E221"),sQuery(id+"F0.wireOp",EDGE,"E222"),sQuery(id+"F0.wireOp",EDGE,"E223"),sQuery(id+"F0.wireOp",EDGE,"E224"),sQuery(id+"F0.wireOp",EDGE,"E225"),sQuery(id+"F0.wireOp",EDGE,"E226"),sQuery(id+"F0.wireOp",EDGE,"E227"),sQuery(id+"F0.wireOp",EDGE,"E228"),sQuery(id+"F0.wireOp",EDGE,"E229"),sQuery(id+"F0.wireOp",EDGE,"E230"),sQuery(id+"F0.wireOp",EDGE,"E231"),sQuery(id+"F0.wireOp",EDGE,"E232"),sQuery(id+"F0.wireOp",EDGE,"E233"),sQuery(id+"F0.wireOp",EDGE,"E444"),sQuery(id+"F0.wireOp",EDGE,"E445"),sQuery(id+"F0.wireOp",EDGE,"E446"),sQuery(id+"F0.wireOp",EDGE,"E447"),sQuery(id+"F0.wireOp",EDGE,"E448"),sQuery(id+"F0.wireOp",EDGE,"E449"),sQuery(id+"F0.wireOp",EDGE,"E450"),sQuery(id+"F0.wireOp",EDGE,"E451"),sQuery(id+"F0.wireOp",EDGE,"E452"),sQuery(id+"F0.wireOp",EDGE,"E453"),sQuery(id+"F0.wireOp",EDGE,"E454"),sQuery(id+"F0.wireOp",EDGE,"E455"),sQuery(id+"F0.wireOp",EDGE,"E456"),sQuery(id+"F0.wireOp",EDGE,"E457"),sQuery(id+"F0.wireOp",EDGE,"E458"),sQuery(id+"F0.wireOp",EDGE,"E459"),sQuery(id+"F0.wireOp",EDGE,"E460"),sQuery(id+"F0.wireOp",EDGE,"E461"),sQuery(id+"F0.wireOp",EDGE,"E462"),sQuery(id+"F0.wireOp",EDGE,"E463"),sQuery(id+"F0.wireOp",EDGE,"E464"),sQuery(id+"F0.wireOp",EDGE,"E465"),sQuery(id+"F0.wireOp",EDGE,"E466"),sQuery(id+"F0.wireOp",EDGE,"E467"),sQuery(id+"F0.wireOp",EDGE,"E468"),sQuery(id+"F0.wireOp",EDGE,"E469"),sQuery(id+"F0.wireOp",EDGE,"E470"),sQuery(id+"F0.wireOp",EDGE,"E499"),sQuery(id+"F0.wireOp",EDGE,"E500"),sQuery(id+"F0.wireOp",EDGE,"E501"),sQuery(id+"F0.wireOp",EDGE,"E502"),sQuery(id+"F0.wireOp",EDGE,"E503"),sQuery(id+"F0.wireOp",EDGE,"E504"),sQuery(id+"F0.wireOp",EDGE,"E505"),sQuery(id+"F0.wireOp",EDGE,"E506"),sQuery(id+"F0.wireOp",EDGE,"E515"),sQuery(id+"F0.wireOp",EDGE,"E516"),sQuery(id+"F0.wireOp",EDGE,"E517"),sQuery(id+"F0.wireOp",EDGE,"E518"),sQuery(id+"F0.wireOp",EDGE,"E519"),sQuery(id+"F0.wireOp",EDGE,"E520"),sQuery(id+"F0.wireOp",EDGE,"E521")])],"isStart":true});
            var sketch = newSketch(context, id + "F2", { "sketchPlane" : qUnion([Q0])});
            skLineSegment(sketch, "E527.bottom", {"start": v(56, -90) * mm, "end": v(-56, -90) * mm});
            skLineSegment(sketch, "E527.top", {"start": v(56, 90) * mm, "end": v(-56, 90) * mm});
            skLineSegment(sketch, "E527.left", {"start": v(56, -90) * mm, "end": v(56, 90) * mm});
            skLineSegment(sketch, "E527.right", {"start": v(-56, -90) * mm, "end": v(-56, 90) * mm});
            skPoint(sketch, "E527.middle", {"position": v(0, 0) * mm});
            skSolve(sketch);
        }
        {
            var Q0;
            Q0 = qSketchRegion(id + "F2", true);
            extrude(context, id + "F3", {"entities" : qUnion([Q0]), "operationType" : NewBodyOperationType.ADD, "depth" : 1 * mm, "offsetDistance" : 25 * mm});
        }
    });
